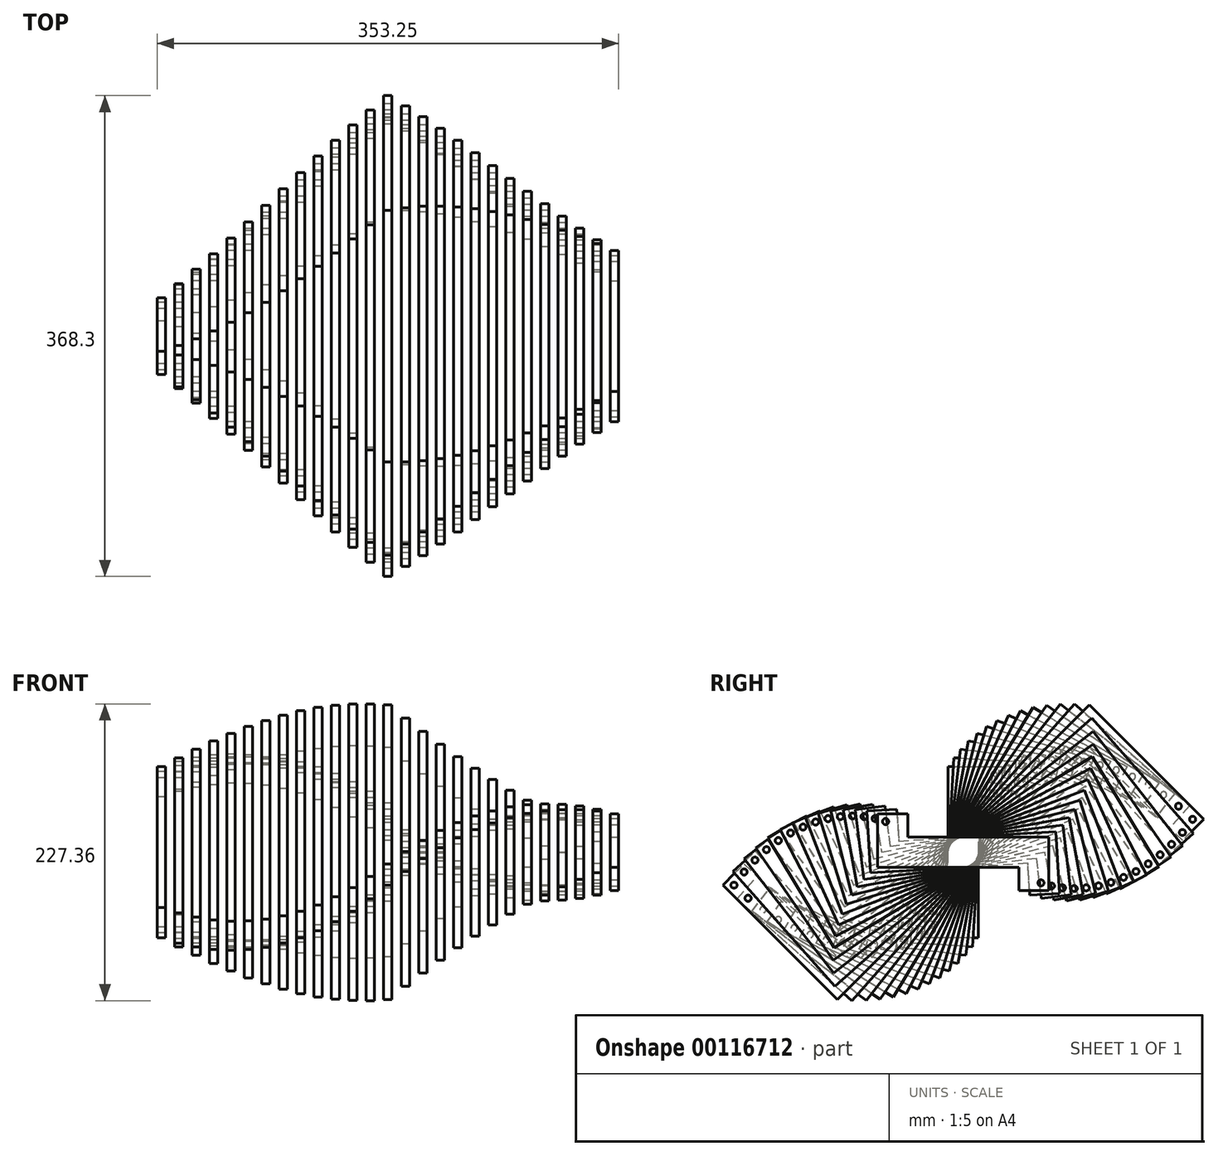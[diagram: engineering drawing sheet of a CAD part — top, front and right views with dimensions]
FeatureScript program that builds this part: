
annotation { "Feature Type Name" : "Feature", "Feature Type Description" : "" }
export const myFeature = defineFeature(function(context is Context, id is Id, definition is map)
    precondition{}
    {
        {
            var Q0;
            Q0=qCreatedBy(makeId("Top.planeOp"),FACE);
            var sketch = newSketch(context, id + "F0", { "sketchPlane" : qUnion([Q0])});
            skLineSegment(sketch, "E0", {"start": v(84.8, 0) * mm, "end": v(-72.92, 0) * mm});
            skSolve(sketch);
        }
        {
            assignVariable(context, id + "F1", {"name" : "Offset", "anyValue" : 13.35});
        }
        {
            assignVariable(context, id + "F2", {"name" : "thick", "anyValue" : 6.35});
        }
        {
            var Q0;
            Q0=qCreatedBy(makeId("Right.planeOp"),FACE);
            var sketch = newSketch(context, id + "F3", { "sketchPlane" : qUnion([Q0])});
            skLineSegment(sketch, "E1", {"start": v(-11.5, 65.5) * mm, "end": v(29.5, 65.5) * mm});
            skLineSegment(sketch, "E2", {"start": v(29.5, 65.5) * mm, "end": v(29.5, 42.5) * mm});
            skLineSegment(sketch, "E3", {"start": v(29.5, 42.5) * mm, "end": v(11.5, 42.5) * mm});
            skLineSegment(sketch, "E4", {"start": v(11.5, 42.5) * mm, "end": v(11.5, -65.5) * mm});
            skLineSegment(sketch, "E5", {"start": v(11.5, -65.5) * mm, "end": v(-29.5, -65.5) * mm});
            skLineSegment(sketch, "E6", {"start": v(-29.5, -65.5) * mm, "end": v(-29.5, -42.5) * mm});
            skLineSegment(sketch, "E7", {"start": v(-29.5, -42.5) * mm, "end": v(-11.5, -42.5) * mm});
            skLineSegment(sketch, "E8", {"start": v(-11.5, -42.5) * mm, "end": v(-11.5, 65.5) * mm});
            skCircle(sketch, "E9", {"center": v(23.5, 59.5) * mm, "radius": 2.35 * mm});
            skLineSegment(sketch, "E10", {"start": v(0, 0) * mm, "end": v(0, 67.87) * mm, "construction": true});
            skCircle(sketch, "E11", {"center": v(-23.5, -59.5) * mm, "radius": 2.35 * mm});
            skSolve(sketch);
        }
        {
            var Q0;
            Q0 = qSketchRegion(id + "F3", true);
            extrude(context, id + "F4", {"entities" : qUnion([Q0]), "depth" : (getVariable(context, 'thick')) * mm});
        }
        {
            var Q0;
            Q0=makeQuery(id+"F4.opExtrude","SWEPT_BODY",BODY,{"disambiguationData":[OSD([sQuery(id+"F3.wireOp",EDGE,"E1"),sQuery(id+"F3.wireOp",EDGE,"E2"),sQuery(id+"F3.wireOp",EDGE,"E3"),sQuery(id+"F3.wireOp",EDGE,"E4"),sQuery(id+"F3.wireOp",EDGE,"E5"),sQuery(id+"F3.wireOp",EDGE,"E6"),sQuery(id+"F3.wireOp",EDGE,"E7"),sQuery(id+"F3.wireOp",EDGE,"E8"),sQuery(id+"F3.wireOp",EDGE,"E9"),sQuery(id+"F3.wireOp",EDGE,"wddxKbAf-IZNn-VG4E-iYQQ-BvLUxmLPDBUU")])]});
            transform(context, id + "F5", {"entities" : qUnion([Q0]), "transformType" : TransformType.TRANSLATION_3D, "dx" : .1 * mm, "dy" : 0 * mm, "dz" : 0 * mm, "makeCopy" : false});
        }
        {
            var Q0;
            Q0=qCreatedBy(makeId("Right.planeOp"),FACE);
            cPlane(context, id + "F6", {"entities" : qUnion([Q0]), "cplaneType" : CPlaneType.OFFSET, "offset" : (getVariable(context, 'Offset')) * mm, "width" : 150 * mm, "height" : 150 * mm});
        }
        {
            var Q0;
            Q0=qCreatedBy(id+"F6.planeOp",FACE);
            var sketch = newSketch(context, id + "F7", { "sketchPlane" : qUnion([Q0])});
            skLineSegment(sketch, "E12", {"start": v(-11.5, 71.85) * mm, "end": v(35.88, 71.85) * mm});
            skLineSegment(sketch, "E13", {"start": v(35.88, 71.85) * mm, "end": v(35.88, 48.85) * mm});
            skLineSegment(sketch, "E14", {"start": v(35.88, 48.85) * mm, "end": v(11.5, 48.85) * mm});
            skLineSegment(sketch, "E15", {"start": v(11.5, 48.85) * mm, "end": v(11.5, -71.85) * mm});
            skLineSegment(sketch, "E16", {"start": v(11.5, -71.85) * mm, "end": v(-35.88, -71.85) * mm});
            skLineSegment(sketch, "E17", {"start": v(-35.88, -71.85) * mm, "end": v(-35.88, -48.84) * mm});
            skLineSegment(sketch, "E18", {"start": v(-35.88, -48.84) * mm, "end": v(-11.5, -48.84) * mm});
            skLineSegment(sketch, "E19", {"start": v(-11.5, -48.84) * mm, "end": v(-11.5, 71.85) * mm});
            skCircle(sketch, "E20", {"center": v(29.88, 65.84) * mm, "radius": 2.35 * mm});
            skCircle(sketch, "E21", {"center": v(-29.88, -65.84) * mm, "radius": 2.35 * mm});
            skSolve(sketch);
        }
        {
            var Q0;
            Q0 = qSketchRegion(id + "F7", true);
            extrude(context, id + "F8", {"entities" : qUnion([Q0]), "depth" : (getVariable(context, 'thick')) * mm});
        }
        {
            var Q0;
            Q0=makeQuery(id+"F8.opExtrude","SWEPT_BODY",BODY,{"disambiguationData":[OSD([sQuery(id+"F7.wireOp",EDGE,"E12"),sQuery(id+"F7.wireOp",EDGE,"E13"),sQuery(id+"F7.wireOp",EDGE,"E14"),sQuery(id+"F7.wireOp",EDGE,"E15"),sQuery(id+"F7.wireOp",EDGE,"E16"),sQuery(id+"F7.wireOp",EDGE,"E17"),sQuery(id+"F7.wireOp",EDGE,"E18"),sQuery(id+"F7.wireOp",EDGE,"E19")])]});
            var Q1;
            Q1=sQuery(id+"F0.wireOp",EDGE,"E0");
            transform(context, id + "F9", {"entities" : qUnion([Q0]), "transformType" : TransformType.ROTATION, "transformAxis" : qUnion([Q1]), "angle" : 3.46 * degree, "makeCopy" : false});
        }
        {
            var Q0;
            Q0=qCreatedBy(id+"F6.planeOp",FACE);
            cPlane(context, id + "F10", {"entities" : qUnion([Q0]), "cplaneType" : CPlaneType.OFFSET, "offset" : (getVariable(context, 'Offset')) * mm, "width" : 150 * mm, "height" : 150 * mm});
        }
        {
            var Q0;
            Q0=qCreatedBy(id+"F10.planeOp",FACE);
            var sketch = newSketch(context, id + "F11", { "sketchPlane" : qUnion([Q0])});
            skLineSegment(sketch, "E22", {"start": v(-11.5, 78.2) * mm, "end": v(42.26, 78.2) * mm});
            skLineSegment(sketch, "E23", {"start": v(42.26, 78.2) * mm, "end": v(42.26, 55.2) * mm});
            skLineSegment(sketch, "E24", {"start": v(42.26, 55.2) * mm, "end": v(11.5, 55.2) * mm});
            skLineSegment(sketch, "E25", {"start": v(11.5, 55.2) * mm, "end": v(11.5, -78.2) * mm});
            skLineSegment(sketch, "E26", {"start": v(11.5, -78.2) * mm, "end": v(-42.26, -78.2) * mm});
            skLineSegment(sketch, "E27", {"start": v(-42.26, -78.2) * mm, "end": v(-42.26, -55.2) * mm});
            skLineSegment(sketch, "E28", {"start": v(-42.26, -55.2) * mm, "end": v(-11.5, -55.2) * mm});
            skLineSegment(sketch, "E29", {"start": v(-11.5, -55.2) * mm, "end": v(-11.5, 78.2) * mm});
            skCircle(sketch, "E30", {"center": v(36.26, 72.2) * mm, "radius": 2.35 * mm});
            skCircle(sketch, "E31", {"center": v(-36.26, -72.2) * mm, "radius": 2.35 * mm});
            skSolve(sketch);
        }
        {
            var Q0;
            Q0 = qSketchRegion(id + "F11", true);
            extrude(context, id + "F12", {"entities" : qUnion([Q0]), "depth" : (getVariable(context, 'thick')) * mm});
        }
        {
            var Q0;
            Q0=makeQuery(id+"F12.opExtrude","SWEPT_BODY",BODY,{"disambiguationData":[OSD([sQuery(id+"F11.wireOp",EDGE,"E22"),sQuery(id+"F11.wireOp",EDGE,"E23"),sQuery(id+"F11.wireOp",EDGE,"E24"),sQuery(id+"F11.wireOp",EDGE,"E25"),sQuery(id+"F11.wireOp",EDGE,"E26"),sQuery(id+"F11.wireOp",EDGE,"E27"),sQuery(id+"F11.wireOp",EDGE,"E28"),sQuery(id+"F11.wireOp",EDGE,"E29")])]});
            var Q1;
            Q1=sQuery(id+"F0.wireOp",EDGE,"E0");
            transform(context, id + "F13", {"entities" : qUnion([Q0]), "transformType" : TransformType.ROTATION, "transformAxis" : qUnion([Q1]), "angle" : 6.92 * degree, "makeCopy" : false});
        }
        {
            var Q0;
            Q0=qCreatedBy(id+"F10.planeOp",FACE);
            cPlane(context, id + "F14", {"entities" : qUnion([Q0]), "cplaneType" : CPlaneType.OFFSET, "offset" : (getVariable(context, 'Offset')) * mm, "width" : 150 * mm, "height" : 150 * mm});
        }
        {
            var Q0;
            Q0=qCreatedBy(id+"F14.planeOp",FACE);
            var sketch = newSketch(context, id + "F15", { "sketchPlane" : qUnion([Q0])});
            skLineSegment(sketch, "E32", {"start": v(-11.5, 84.53) * mm, "end": v(48.64, 84.53) * mm});
            skLineSegment(sketch, "E33", {"start": v(48.64, 84.53) * mm, "end": v(48.64, 61.54) * mm});
            skLineSegment(sketch, "E34", {"start": v(48.64, 61.54) * mm, "end": v(11.5, 61.54) * mm});
            skLineSegment(sketch, "E35", {"start": v(11.5, 61.54) * mm, "end": v(11.5, -84.53) * mm});
            skLineSegment(sketch, "E36", {"start": v(11.5, -84.53) * mm, "end": v(-48.64, -84.53) * mm});
            skLineSegment(sketch, "E37", {"start": v(-48.64, -84.53) * mm, "end": v(-48.64, -61.54) * mm});
            skLineSegment(sketch, "E38", {"start": v(-48.64, -61.54) * mm, "end": v(-11.5, -61.54) * mm});
            skLineSegment(sketch, "E39", {"start": v(-11.5, -61.53) * mm, "end": v(-11.5, 84.53) * mm});
            skCircle(sketch, "E40", {"center": v(42.64, 78.53) * mm, "radius": 2.35 * mm});
            skCircle(sketch, "E41", {"center": v(-42.64, -78.53) * mm, "radius": 2.35 * mm});
            skSolve(sketch);
        }
        {
            var Q0;
            Q0 = qSketchRegion(id + "F15", true);
            extrude(context, id + "F16", {"entities" : qUnion([Q0]), "depth" : (getVariable(context, 'thick')) * mm});
        }
        {
            var Q0;
            Q0=makeQuery(id+"F16.opExtrude","SWEPT_BODY",BODY,{"disambiguationData":[OSD([sQuery(id+"F15.wireOp",EDGE,"E32"),sQuery(id+"F15.wireOp",EDGE,"E33"),sQuery(id+"F15.wireOp",EDGE,"E34"),sQuery(id+"F15.wireOp",EDGE,"E35"),sQuery(id+"F15.wireOp",EDGE,"E36"),sQuery(id+"F15.wireOp",EDGE,"E37"),sQuery(id+"F15.wireOp",EDGE,"E38"),sQuery(id+"F15.wireOp",EDGE,"E39"),sQuery(id+"F15.wireOp",EDGE,"E40")])]});
            var Q1;
            Q1=sQuery(id+"F0.wireOp",EDGE,"E0");
            transform(context, id + "F17", {"entities" : qUnion([Q0]), "transformType" : TransformType.ROTATION, "transformAxis" : qUnion([Q1]), "angle" : 10.38 * degree, "makeCopy" : false});
        }
        {
            var Q0;
            Q0=qCreatedBy(id+"F14.planeOp",FACE);
            cPlane(context, id + "F18", {"entities" : qUnion([Q0]), "cplaneType" : CPlaneType.OFFSET, "offset" : (getVariable(context, 'Offset')) * mm, "width" : 150 * mm, "height" : 150 * mm});
        }
        {
            var Q0;
            Q0=qCreatedBy(id+"F18.planeOp",FACE);
            var sketch = newSketch(context, id + "F19", { "sketchPlane" : qUnion([Q0])});
            skLineSegment(sketch, "E42", {"start": v(-11.5, 90.89) * mm, "end": v(55.02, 90.89) * mm});
            skLineSegment(sketch, "E43", {"start": v(55.02, 90.88) * mm, "end": v(55.02, 67.89) * mm});
            skLineSegment(sketch, "E44", {"start": v(55.02, 67.89) * mm, "end": v(11.5, 67.89) * mm});
            skLineSegment(sketch, "E45", {"start": v(11.5, 67.89) * mm, "end": v(11.5, -90.89) * mm});
            skLineSegment(sketch, "E46", {"start": v(11.5, -90.89) * mm, "end": v(-55.02, -90.89) * mm});
            skLineSegment(sketch, "E47", {"start": v(-55.02, -90.89) * mm, "end": v(-55.02, -67.89) * mm});
            skLineSegment(sketch, "E48", {"start": v(-55.02, -67.89) * mm, "end": v(-11.5, -67.89) * mm});
            skLineSegment(sketch, "E49", {"start": v(-11.5, -67.89) * mm, "end": v(-11.5, 90.89) * mm});
            skCircle(sketch, "E50", {"center": v(49.02, 84.89) * mm, "radius": 2.35 * mm});
            skCircle(sketch, "E51", {"center": v(-49.02, -84.89) * mm, "radius": 2.35 * mm});
            skSolve(sketch);
        }
        {
            var Q0;
            Q0 = qSketchRegion(id + "F19", true);
            extrude(context, id + "F20", {"entities" : qUnion([Q0]), "depth" : (getVariable(context, 'thick')) * mm});
        }
        {
            var Q0;
            Q0=makeQuery(id+"F20.opExtrude","SWEPT_BODY",BODY,{"disambiguationData":[OSD([sQuery(id+"F19.wireOp",EDGE,"E42"),sQuery(id+"F19.wireOp",EDGE,"E43"),sQuery(id+"F19.wireOp",EDGE,"E44"),sQuery(id+"F19.wireOp",EDGE,"E45"),sQuery(id+"F19.wireOp",EDGE,"E46"),sQuery(id+"F19.wireOp",EDGE,"E47"),sQuery(id+"F19.wireOp",EDGE,"E48"),sQuery(id+"F19.wireOp",EDGE,"E49"),sQuery(id+"F19.wireOp",EDGE,"E50")])]});
            var Q1;
            Q1=sQuery(id+"F0.wireOp",EDGE,"E0");
            transform(context, id + "F21", {"entities" : qUnion([Q0]), "transformType" : TransformType.ROTATION, "transformAxis" : qUnion([Q1]), "angle" : 13.84 * degree, "makeCopy" : false});
        }
        {
            var Q0;
            Q0=qCreatedBy(id+"F18.planeOp",FACE);
            cPlane(context, id + "F22", {"entities" : qUnion([Q0]), "cplaneType" : CPlaneType.OFFSET, "offset" : (getVariable(context, 'Offset')) * mm, "width" : 150 * mm, "height" : 150 * mm});
        }
        {
            var Q0;
            Q0=qCreatedBy(id+"F22.planeOp",FACE);
            var sketch = newSketch(context, id + "F23", { "sketchPlane" : qUnion([Q0])});
            skLineSegment(sketch, "E52", {"start": v(-11.5, 97.23) * mm, "end": v(61.4, 97.23) * mm});
            skLineSegment(sketch, "E53", {"start": v(61.4, 97.23) * mm, "end": v(61.4, 74.23) * mm});
            skLineSegment(sketch, "E54", {"start": v(61.4, 74.23) * mm, "end": v(11.5, 74.23) * mm});
            skLineSegment(sketch, "E55", {"start": v(11.5, 74.23) * mm, "end": v(11.5, -97.23) * mm});
            skLineSegment(sketch, "E56", {"start": v(11.5, -97.23) * mm, "end": v(-61.4, -97.23) * mm});
            skLineSegment(sketch, "E57", {"start": v(-61.4, -97.23) * mm, "end": v(-61.4, -74.23) * mm});
            skLineSegment(sketch, "E58", {"start": v(-61.4, -74.23) * mm, "end": v(-11.5, -74.23) * mm});
            skLineSegment(sketch, "E59", {"start": v(-11.5, -74.23) * mm, "end": v(-11.5, 97.23) * mm});
            skCircle(sketch, "E60", {"center": v(55.4, 91.23) * mm, "radius": 2.35 * mm});
            skCircle(sketch, "E61", {"center": v(-55.4, -91.23) * mm, "radius": 2.35 * mm});
            skSolve(sketch);
        }
        {
            var Q0;
            Q0 = qSketchRegion(id + "F23", true);
            extrude(context, id + "F24", {"entities" : qUnion([Q0]), "depth" : (getVariable(context, 'thick')) * mm});
        }
        {
            var Q0;
            Q0=makeQuery(id+"F24.opExtrude","SWEPT_BODY",BODY,{"disambiguationData":[OSD([sQuery(id+"F23.wireOp",EDGE,"E52"),sQuery(id+"F23.wireOp",EDGE,"E53"),sQuery(id+"F23.wireOp",EDGE,"E54"),sQuery(id+"F23.wireOp",EDGE,"E55"),sQuery(id+"F23.wireOp",EDGE,"E56"),sQuery(id+"F23.wireOp",EDGE,"E57"),sQuery(id+"F23.wireOp",EDGE,"E58"),sQuery(id+"F23.wireOp",EDGE,"E59"),sQuery(id+"F23.wireOp",EDGE,"E60")])]});
            var Q1;
            Q1=sQuery(id+"F0.wireOp",EDGE,"E0");
            transform(context, id + "F25", {"entities" : qUnion([Q0]), "transformType" : TransformType.ROTATION, "transformAxis" : qUnion([Q1]), "angle" : 17.3 * degree, "makeCopy" : false});
        }
        {
            var Q0;
            Q0=qCreatedBy(id+"F22.planeOp",FACE);
            cPlane(context, id + "F26", {"entities" : qUnion([Q0]), "cplaneType" : CPlaneType.OFFSET, "offset" : (getVariable(context, 'Offset')) * mm, "width" : 150 * mm, "height" : 150 * mm});
        }
        {
            var Q0;
            Q0=qCreatedBy(id+"F26.planeOp",FACE);
            var sketch = newSketch(context, id + "F27", { "sketchPlane" : qUnion([Q0])});
            skLineSegment(sketch, "E62", {"start": v(-11.5, 103.58) * mm, "end": v(67.78, 103.58) * mm});
            skLineSegment(sketch, "E63", {"start": v(67.78, 103.58) * mm, "end": v(67.78, 80.57) * mm});
            skLineSegment(sketch, "E64", {"start": v(67.78, 80.57) * mm, "end": v(11.5, 80.57) * mm});
            skLineSegment(sketch, "E65", {"start": v(11.5, 80.57) * mm, "end": v(11.5, -103.58) * mm});
            skLineSegment(sketch, "E66", {"start": v(11.5, -103.58) * mm, "end": v(-67.78, -103.58) * mm});
            skLineSegment(sketch, "E67", {"start": v(-67.78, -103.58) * mm, "end": v(-67.78, -80.57) * mm});
            skLineSegment(sketch, "E68", {"start": v(-67.78, -80.57) * mm, "end": v(-11.5, -80.57) * mm});
            skLineSegment(sketch, "E69", {"start": v(-11.5, -80.57) * mm, "end": v(-11.5, 103.58) * mm});
            skCircle(sketch, "E70", {"center": v(61.78, 97.58) * mm, "radius": 2.35 * mm});
            skCircle(sketch, "E71", {"center": v(-61.78, -97.58) * mm, "radius": 2.35 * mm});
            skSolve(sketch);
        }
        {
            var Q0;
            Q0 = qSketchRegion(id + "F27", true);
            extrude(context, id + "F28", {"entities" : qUnion([Q0]), "depth" : (getVariable(context, 'thick')) * mm});
        }
        {
            var Q0;
            Q0=makeQuery(id+"F28.opExtrude","SWEPT_BODY",BODY,{"disambiguationData":[OSD([sQuery(id+"F27.wireOp",EDGE,"E62"),sQuery(id+"F27.wireOp",EDGE,"E63"),sQuery(id+"F27.wireOp",EDGE,"E64"),sQuery(id+"F27.wireOp",EDGE,"E65"),sQuery(id+"F27.wireOp",EDGE,"E66"),sQuery(id+"F27.wireOp",EDGE,"E67"),sQuery(id+"F27.wireOp",EDGE,"E68"),sQuery(id+"F27.wireOp",EDGE,"E69"),sQuery(id+"F27.wireOp",EDGE,"E70")])]});
            var Q1;
            Q1=sQuery(id+"F0.wireOp",EDGE,"E0");
            transform(context, id + "F29", {"entities" : qUnion([Q0]), "transformType" : TransformType.ROTATION, "transformAxis" : qUnion([Q1]), "angle" : 20.76 * degree, "makeCopy" : false});
        }
        {
            var Q0;
            Q0=qCreatedBy(id+"F26.planeOp",FACE);
            cPlane(context, id + "F30", {"entities" : qUnion([Q0]), "cplaneType" : CPlaneType.OFFSET, "offset" : (getVariable(context, 'Offset')) * mm, "width" : 150 * mm, "height" : 150 * mm});
        }
        {
            var Q0;
            Q0=qCreatedBy(id+"F30.planeOp",FACE);
            var sketch = newSketch(context, id + "F31", { "sketchPlane" : qUnion([Q0])});
            skLineSegment(sketch, "E72", {"start": v(-11.5, 109.92) * mm, "end": v(74.16, 109.92) * mm});
            skLineSegment(sketch, "E73", {"start": v(74.16, 109.92) * mm, "end": v(74.16, 86.92) * mm});
            skLineSegment(sketch, "E74", {"start": v(74.16, 86.92) * mm, "end": v(11.5, 86.92) * mm});
            skLineSegment(sketch, "E75", {"start": v(11.5, 86.92) * mm, "end": v(11.5, -109.92) * mm});
            skLineSegment(sketch, "E76", {"start": v(11.5, -109.92) * mm, "end": v(-74.16, -109.92) * mm});
            skLineSegment(sketch, "E77", {"start": v(-74.16, -109.92) * mm, "end": v(-74.16, -86.92) * mm});
            skLineSegment(sketch, "E78", {"start": v(-74.16, -86.92) * mm, "end": v(-11.5, -86.92) * mm});
            skLineSegment(sketch, "E79", {"start": v(-11.5, -86.92) * mm, "end": v(-11.5, 109.92) * mm});
            skCircle(sketch, "E80", {"center": v(68.16, 103.92) * mm, "radius": 2.35 * mm});
            skCircle(sketch, "E81", {"center": v(-68.16, -103.92) * mm, "radius": 2.35 * mm});
            skSolve(sketch);
        }
        {
            var Q0;
            Q0 = qSketchRegion(id + "F31", true);
            extrude(context, id + "F32", {"entities" : qUnion([Q0]), "depth" : (getVariable(context, 'thick')) * mm});
        }
        {
            var Q0;
            Q0=makeQuery(id+"F32.opExtrude","SWEPT_BODY",BODY,{"disambiguationData":[OSD([sQuery(id+"F31.wireOp",EDGE,"E72"),sQuery(id+"F31.wireOp",EDGE,"E73"),sQuery(id+"F31.wireOp",EDGE,"E74"),sQuery(id+"F31.wireOp",EDGE,"E75"),sQuery(id+"F31.wireOp",EDGE,"E76"),sQuery(id+"F31.wireOp",EDGE,"E77"),sQuery(id+"F31.wireOp",EDGE,"E78"),sQuery(id+"F31.wireOp",EDGE,"E79"),sQuery(id+"F31.wireOp",EDGE,"E80")])]});
            var Q1;
            Q1=sQuery(id+"F0.wireOp",EDGE,"E0");
            transform(context, id + "F33", {"entities" : qUnion([Q0]), "transformType" : TransformType.ROTATION, "transformAxis" : qUnion([Q1]), "angle" : 24.22 * degree, "makeCopy" : false});
        }
        {
            var Q0;
            Q0=qCreatedBy(id+"F30.planeOp",FACE);
            cPlane(context, id + "F34", {"entities" : qUnion([Q0]), "cplaneType" : CPlaneType.OFFSET, "offset" : (getVariable(context, 'Offset')) * mm, "width" : 150 * mm, "height" : 150 * mm});
        }
        {
            var Q0;
            Q0=qCreatedBy(id+"F34.planeOp",FACE);
            var sketch = newSketch(context, id + "F35", { "sketchPlane" : qUnion([Q0])});
            skLineSegment(sketch, "E82", {"start": v(-11.5, 116.27) * mm, "end": v(80.54, 116.27) * mm});
            skLineSegment(sketch, "E83", {"start": v(80.54, 116.27) * mm, "end": v(80.54, 93.27) * mm});
            skLineSegment(sketch, "E84", {"start": v(80.54, 93.27) * mm, "end": v(11.5, 93.27) * mm});
            skLineSegment(sketch, "E85", {"start": v(11.5, 93.27) * mm, "end": v(11.5, -116.27) * mm});
            skLineSegment(sketch, "E86", {"start": v(11.5, -116.27) * mm, "end": v(-80.54, -116.27) * mm});
            skLineSegment(sketch, "E87", {"start": v(-80.54, -116.27) * mm, "end": v(-80.54, -93.27) * mm});
            skLineSegment(sketch, "E88", {"start": v(-80.54, -93.27) * mm, "end": v(-11.5, -93.27) * mm});
            skLineSegment(sketch, "E89", {"start": v(-11.5, -93.27) * mm, "end": v(-11.5, 116.27) * mm});
            skCircle(sketch, "E90", {"center": v(74.54, 110.27) * mm, "radius": 2.35 * mm});
            skCircle(sketch, "E91", {"center": v(-74.54, -110.27) * mm, "radius": 2.35 * mm});
            skSolve(sketch);
        }
        {
            var Q0;
            Q0 = qSketchRegion(id + "F35", true);
            extrude(context, id + "F36", {"entities" : qUnion([Q0]), "depth" : (getVariable(context, 'thick')) * mm});
        }
        {
            var Q0;
            Q0=makeQuery(id+"F36.opExtrude","SWEPT_BODY",BODY,{"disambiguationData":[OSD([sQuery(id+"F35.wireOp",EDGE,"E82"),sQuery(id+"F35.wireOp",EDGE,"E83"),sQuery(id+"F35.wireOp",EDGE,"E84"),sQuery(id+"F35.wireOp",EDGE,"E85"),sQuery(id+"F35.wireOp",EDGE,"E86"),sQuery(id+"F35.wireOp",EDGE,"E87"),sQuery(id+"F35.wireOp",EDGE,"E88"),sQuery(id+"F35.wireOp",EDGE,"E89"),sQuery(id+"F35.wireOp",EDGE,"E90")])]});
            var Q1;
            Q1=sQuery(id+"F0.wireOp",EDGE,"E0");
            transform(context, id + "F37", {"entities" : qUnion([Q0]), "transformType" : TransformType.ROTATION, "transformAxis" : qUnion([Q1]), "angle" : 27.68 * degree, "makeCopy" : false});
        }
        {
            var Q0;
            Q0=qCreatedBy(id+"F34.planeOp",FACE);
            cPlane(context, id + "F38", {"entities" : qUnion([Q0]), "cplaneType" : CPlaneType.OFFSET, "offset" : (getVariable(context, 'Offset')) * mm, "width" : 150 * mm, "height" : 150 * mm});
        }
        {
            var Q0;
            Q0=qCreatedBy(id+"F38.planeOp",FACE);
            var sketch = newSketch(context, id + "F39", { "sketchPlane" : qUnion([Q0])});
            skLineSegment(sketch, "E92", {"start": v(-11.5, 122.61) * mm, "end": v(86.92, 122.61) * mm});
            skLineSegment(sketch, "E93", {"start": v(86.92, 122.61) * mm, "end": v(86.92, 99.62) * mm});
            skLineSegment(sketch, "E94", {"start": v(86.92, 99.62) * mm, "end": v(11.5, 99.61) * mm});
            skLineSegment(sketch, "E95", {"start": v(11.5, 99.61) * mm, "end": v(11.5, -122.61) * mm});
            skLineSegment(sketch, "E96", {"start": v(11.5, -122.61) * mm, "end": v(-86.92, -122.62) * mm});
            skLineSegment(sketch, "E97", {"start": v(-86.92, -122.62) * mm, "end": v(-86.92, -99.61) * mm});
            skLineSegment(sketch, "E98", {"start": v(-86.92, -99.61) * mm, "end": v(-11.5, -99.61) * mm});
            skLineSegment(sketch, "E99", {"start": v(-11.5, -99.61) * mm, "end": v(-11.5, 122.62) * mm});
            skCircle(sketch, "E100", {"center": v(80.92, 116.61) * mm, "radius": 2.35 * mm});
            skCircle(sketch, "E101", {"center": v(-80.92, -116.62) * mm, "radius": 2.35 * mm});
            skSolve(sketch);
        }
        {
            var Q0;
            Q0 = qSketchRegion(id + "F39", true);
            extrude(context, id + "F40", {"entities" : qUnion([Q0]), "depth" : (getVariable(context, 'thick')) * mm});
        }
        {
            var Q0;
            Q0=makeQuery(id+"F40.opExtrude","SWEPT_BODY",BODY,{"disambiguationData":[OSD([sQuery(id+"F39.wireOp",EDGE,"E92"),sQuery(id+"F39.wireOp",EDGE,"E93"),sQuery(id+"F39.wireOp",EDGE,"E94"),sQuery(id+"F39.wireOp",EDGE,"E95"),sQuery(id+"F39.wireOp",EDGE,"E96"),sQuery(id+"F39.wireOp",EDGE,"E97"),sQuery(id+"F39.wireOp",EDGE,"E98"),sQuery(id+"F39.wireOp",EDGE,"E99"),sQuery(id+"F39.wireOp",EDGE,"E100")])]});
            var Q1;
            Q1=sQuery(id+"F0.wireOp",EDGE,"E0");
            transform(context, id + "F41", {"entities" : qUnion([Q0]), "transformType" : TransformType.ROTATION, "transformAxis" : qUnion([Q1]), "angle" : 31.14 * degree, "makeCopy" : false});
        }
        {
            var Q0;
            Q0=qCreatedBy(id+"F38.planeOp",FACE);
            cPlane(context, id + "F42", {"entities" : qUnion([Q0]), "cplaneType" : CPlaneType.OFFSET, "offset" : (getVariable(context, 'Offset')) * mm, "width" : 150 * mm, "height" : 150 * mm});
        }
        {
            var Q0;
            Q0=qCreatedBy(id+"F42.planeOp",FACE);
            var sketch = newSketch(context, id + "F43", { "sketchPlane" : qUnion([Q0])});
            skLineSegment(sketch, "E102", {"start": v(-11.5, 128.96) * mm, "end": v(93.3, 128.96) * mm});
            skLineSegment(sketch, "E103", {"start": v(93.3, 128.96) * mm, "end": v(93.3, 105.96) * mm});
            skLineSegment(sketch, "E104", {"start": v(93.3, 105.96) * mm, "end": v(11.5, 105.96) * mm});
            skLineSegment(sketch, "E105", {"start": v(11.5, 105.96) * mm, "end": v(11.5, -128.96) * mm});
            skLineSegment(sketch, "E106", {"start": v(11.5, -128.96) * mm, "end": v(-93.3, -128.96) * mm});
            skLineSegment(sketch, "E107", {"start": v(-93.3, -128.96) * mm, "end": v(-93.3, -105.96) * mm});
            skLineSegment(sketch, "E108", {"start": v(-93.3, -105.96) * mm, "end": v(-11.5, -105.96) * mm});
            skLineSegment(sketch, "E109", {"start": v(-11.5, -105.96) * mm, "end": v(-11.5, 128.96) * mm});
            skCircle(sketch, "E110", {"center": v(87.3, 122.96) * mm, "radius": 2.35 * mm});
            skCircle(sketch, "E111", {"center": v(-87.3, -122.96) * mm, "radius": 2.35 * mm});
            skSolve(sketch);
        }
        {
            var Q0;
            Q0 = qSketchRegion(id + "F43", true);
            extrude(context, id + "F44", {"entities" : qUnion([Q0]), "depth" : (getVariable(context, 'thick')) * mm});
        }
        {
            var Q0;
            Q0=makeQuery(id+"F44.opExtrude","SWEPT_BODY",BODY,{"disambiguationData":[OSD([sQuery(id+"F43.wireOp",EDGE,"E102"),sQuery(id+"F43.wireOp",EDGE,"E103"),sQuery(id+"F43.wireOp",EDGE,"E104"),sQuery(id+"F43.wireOp",EDGE,"E105"),sQuery(id+"F43.wireOp",EDGE,"E106"),sQuery(id+"F43.wireOp",EDGE,"E107"),sQuery(id+"F43.wireOp",EDGE,"E108"),sQuery(id+"F43.wireOp",EDGE,"E109"),sQuery(id+"F43.wireOp",EDGE,"E110")])]});
            var Q1;
            Q1=sQuery(id+"F0.wireOp",EDGE,"E0");
            transform(context, id + "F45", {"entities" : qUnion([Q0]), "transformType" : TransformType.ROTATION, "transformAxis" : qUnion([Q1]), "angle" : 34.6 * degree, "makeCopy" : false});
        }
        {
            var Q0;
            Q0=qCreatedBy(id+"F42.planeOp",FACE);
            cPlane(context, id + "F46", {"entities" : qUnion([Q0]), "cplaneType" : CPlaneType.OFFSET, "offset" : (getVariable(context, 'Offset')) * mm, "width" : 150 * mm, "height" : 150 * mm});
        }
        {
            var Q0;
            Q0=qCreatedBy(id+"F46.planeOp",FACE);
            var sketch = newSketch(context, id + "F47", { "sketchPlane" : qUnion([Q0])});
            skLineSegment(sketch, "E112", {"start": v(-11.5, 135.3) * mm, "end": v(99.68, 135.3) * mm});
            skLineSegment(sketch, "E113", {"start": v(99.68, 135.3) * mm, "end": v(99.68, 112.3) * mm});
            skLineSegment(sketch, "E114", {"start": v(99.68, 112.3) * mm, "end": v(11.5, 112.3) * mm});
            skLineSegment(sketch, "E115", {"start": v(11.5, 112.3) * mm, "end": v(11.5, -135.3) * mm});
            skLineSegment(sketch, "E116", {"start": v(11.5, -135.3) * mm, "end": v(-99.68, -135.3) * mm});
            skLineSegment(sketch, "E117", {"start": v(-99.68, -135.3) * mm, "end": v(-99.68, -112.3) * mm});
            skLineSegment(sketch, "E118", {"start": v(-99.68, -112.3) * mm, "end": v(-11.5, -112.3) * mm});
            skLineSegment(sketch, "E119", {"start": v(-11.5, -112.3) * mm, "end": v(-11.5, 135.3) * mm});
            skCircle(sketch, "E120", {"center": v(93.68, 129.3) * mm, "radius": 2.35 * mm});
            skCircle(sketch, "E121", {"center": v(-93.68, -129.3) * mm, "radius": 2.35 * mm});
            skSolve(sketch);
        }
        {
            var Q0;
            Q0 = qSketchRegion(id + "F47", true);
            extrude(context, id + "F48", {"entities" : qUnion([Q0]), "depth" : (getVariable(context, 'thick')) * mm});
        }
        {
            var Q0;
            Q0=makeQuery(id+"F48.opExtrude","SWEPT_BODY",BODY,{"disambiguationData":[OSD([sQuery(id+"F47.wireOp",EDGE,"E112"),sQuery(id+"F47.wireOp",EDGE,"E113"),sQuery(id+"F47.wireOp",EDGE,"E114"),sQuery(id+"F47.wireOp",EDGE,"E115"),sQuery(id+"F47.wireOp",EDGE,"E116"),sQuery(id+"F47.wireOp",EDGE,"E117"),sQuery(id+"F47.wireOp",EDGE,"E118"),sQuery(id+"F47.wireOp",EDGE,"E119"),sQuery(id+"F47.wireOp",EDGE,"E120"),sQuery(id+"F47.wireOp",EDGE,"E121")])]});
            var Q1;
            Q1=sQuery(id+"F0.wireOp",EDGE,"E0");
            transform(context, id + "F49", {"entities" : qUnion([Q0]), "transformType" : TransformType.ROTATION, "transformAxis" : qUnion([Q1]), "angle" : 38.06 * degree, "makeCopy" : false});
        }
        {
            var Q0;
            Q0=qCreatedBy(id+"F46.planeOp",FACE);
            cPlane(context, id + "F50", {"entities" : qUnion([Q0]), "cplaneType" : CPlaneType.OFFSET, "offset" : (getVariable(context, 'Offset')) * mm, "width" : 150 * mm, "height" : 150 * mm});
        }
        {
            var Q0;
            Q0=qCreatedBy(id+"F50.planeOp",FACE);
            var sketch = newSketch(context, id + "F51", { "sketchPlane" : qUnion([Q0])});
            skLineSegment(sketch, "E122", {"start": v(-11.5, 141.65) * mm, "end": v(106.06, 141.65) * mm});
            skLineSegment(sketch, "E123", {"start": v(106.06, 141.65) * mm, "end": v(106.06, 118.65) * mm});
            skLineSegment(sketch, "E124", {"start": v(106.06, 118.65) * mm, "end": v(11.5, 118.65) * mm});
            skLineSegment(sketch, "E125", {"start": v(11.5, 118.65) * mm, "end": v(11.5, -141.65) * mm});
            skLineSegment(sketch, "E126", {"start": v(11.5, -141.65) * mm, "end": v(-106.06, -141.65) * mm});
            skLineSegment(sketch, "E127", {"start": v(-106.06, -141.65) * mm, "end": v(-106.06, -118.65) * mm});
            skLineSegment(sketch, "E128", {"start": v(-106.06, -118.65) * mm, "end": v(-11.5, -118.65) * mm});
            skLineSegment(sketch, "E129", {"start": v(-11.5, -118.65) * mm, "end": v(-11.5, 141.65) * mm});
            skCircle(sketch, "E130", {"center": v(100.06, 135.65) * mm, "radius": 2.35 * mm});
            skCircle(sketch, "E131", {"center": v(-100.06, -135.65) * mm, "radius": 2.35 * mm});
            skSolve(sketch);
        }
        {
            var Q0;
            Q0 = qSketchRegion(id + "F51", true);
            extrude(context, id + "F52", {"entities" : qUnion([Q0]), "depth" : (getVariable(context, 'thick')) * mm});
        }
        {
            var Q0;
            Q0=makeQuery(id+"F52.opExtrude","SWEPT_BODY",BODY,{"disambiguationData":[OSD([sQuery(id+"F51.wireOp",EDGE,"E122"),sQuery(id+"F51.wireOp",EDGE,"E123"),sQuery(id+"F51.wireOp",EDGE,"E124"),sQuery(id+"F51.wireOp",EDGE,"E125"),sQuery(id+"F51.wireOp",EDGE,"E126"),sQuery(id+"F51.wireOp",EDGE,"E127"),sQuery(id+"F51.wireOp",EDGE,"E128"),sQuery(id+"F51.wireOp",EDGE,"E129"),sQuery(id+"F51.wireOp",EDGE,"E130"),sQuery(id+"F51.wireOp",EDGE,"E131")])]});
            var Q1;
            Q1=sQuery(id+"F0.wireOp",EDGE,"E0");
            transform(context, id + "F53", {"entities" : qUnion([Q0]), "transformType" : TransformType.ROTATION, "transformAxis" : qUnion([Q1]), "angle" : 41.52 * degree, "makeCopy" : false});
        }
        {
            var Q0;
            Q0=qCreatedBy(id+"F50.planeOp",FACE);
            cPlane(context, id + "F54", {"entities" : qUnion([Q0]), "cplaneType" : CPlaneType.OFFSET, "offset" : (getVariable(context, 'Offset')) * mm, "width" : 150 * mm, "height" : 150 * mm});
        }
        {
            var Q0;
            Q0=qCreatedBy(id+"F54.planeOp",FACE);
            var sketch = newSketch(context, id + "F55", { "sketchPlane" : qUnion([Q0])});
            skLineSegment(sketch, "E132", {"start": v(-11.5, 148) * mm, "end": v(112.44, 148) * mm});
            skLineSegment(sketch, "E133", {"start": v(112.44, 148) * mm, "end": v(112.44, 125) * mm});
            skLineSegment(sketch, "E134", {"start": v(112.44, 125) * mm, "end": v(11.5, 125) * mm});
            skLineSegment(sketch, "E135", {"start": v(11.5, 125) * mm, "end": v(11.5, -148) * mm});
            skLineSegment(sketch, "E136", {"start": v(11.5, -148) * mm, "end": v(-112.44, -148) * mm});
            skLineSegment(sketch, "E137", {"start": v(-112.44, -148) * mm, "end": v(-112.44, -125) * mm});
            skLineSegment(sketch, "E138", {"start": v(-112.44, -125) * mm, "end": v(-11.5, -125) * mm});
            skLineSegment(sketch, "E139", {"start": v(-11.5, -125) * mm, "end": v(-11.5, 148) * mm});
            skCircle(sketch, "E140", {"center": v(106.44, 142) * mm, "radius": 2.35 * mm});
            skCircle(sketch, "E141", {"center": v(-106.44, -142) * mm, "radius": 2.35 * mm});
            skSolve(sketch);
        }
        {
            var Q0;
            Q0 = qSketchRegion(id + "F55", true);
            extrude(context, id + "F56", {"entities" : qUnion([Q0]), "depth" : (getVariable(context, 'thick')) * mm});
        }
        {
            var Q0;
            Q0=makeQuery(id+"F56.opExtrude","SWEPT_BODY",BODY,{"disambiguationData":[OSD([sQuery(id+"F55.wireOp",EDGE,"E132"),sQuery(id+"F55.wireOp",EDGE,"E133"),sQuery(id+"F55.wireOp",EDGE,"E134"),sQuery(id+"F55.wireOp",EDGE,"E135"),sQuery(id+"F55.wireOp",EDGE,"E136"),sQuery(id+"F55.wireOp",EDGE,"E137"),sQuery(id+"F55.wireOp",EDGE,"E138"),sQuery(id+"F55.wireOp",EDGE,"E139"),sQuery(id+"F55.wireOp",EDGE,"E140"),sQuery(id+"F55.wireOp",EDGE,"E141")])]});
            var Q1;
            Q1=sQuery(id+"F0.wireOp",EDGE,"E0");
            transform(context, id + "F57", {"entities" : qUnion([Q0]), "transformType" : TransformType.ROTATION, "transformAxis" : qUnion([Q1]), "angle" : 44.98 * degree, "makeCopy" : false});
        }
        {
            var Q0;
            Q0=makeQuery(id+"F56.opExtrude","CAP_FACE",FACE,{"disambiguationData":[OSD([sQuery(id+"F55.wireOp",EDGE,"E132"),sQuery(id+"F55.wireOp",EDGE,"E133"),sQuery(id+"F55.wireOp",EDGE,"E134"),sQuery(id+"F55.wireOp",EDGE,"E135"),sQuery(id+"F55.wireOp",EDGE,"E136"),sQuery(id+"F55.wireOp",EDGE,"E137"),sQuery(id+"F55.wireOp",EDGE,"E138"),sQuery(id+"F55.wireOp",EDGE,"E139"),sQuery(id+"F55.wireOp",EDGE,"E140"),sQuery(id+"F55.wireOp",EDGE,"E141")])],"isStart":false});
            cPlane(context, id + "F58", {"entities" : qUnion([Q0]), "cplaneType" : CPlaneType.OFFSET, "offset" : (getVariable(context, 'thick') / 2) * mm, "oppositeDirection" : true, "width" : 150 * mm, "height" : 150 * mm});
        }
        {
            var Q0;
            Q0=makeQuery(id+"F52.opExtrude","SWEPT_BODY",BODY,{"disambiguationData":[OSD([sQuery(id+"F51.wireOp",EDGE,"E122"),sQuery(id+"F51.wireOp",EDGE,"E123"),sQuery(id+"F51.wireOp",EDGE,"E124"),sQuery(id+"F51.wireOp",EDGE,"E125"),sQuery(id+"F51.wireOp",EDGE,"E126"),sQuery(id+"F51.wireOp",EDGE,"E127"),sQuery(id+"F51.wireOp",EDGE,"E128"),sQuery(id+"F51.wireOp",EDGE,"E129"),sQuery(id+"F51.wireOp",EDGE,"E130"),sQuery(id+"F51.wireOp",EDGE,"E131")])]});
            var Q1;
            Q1=qCreatedBy(id+"F58.planeOp",FACE);
            mirror(context, id + "F59", {"entities" : qUnion([Q0]), "mirrorPlane" : qUnion([Q1])});
        }
        {
            var Q0;
            Q0=makeQuery(id+"F59.opPattern","COPY",BODY,{"derivedFrom":makeQuery(id+"F52.opExtrude","SWEPT_BODY",BODY,{"disambiguationData":[OSD([sQuery(id+"F51.wireOp",EDGE,"E122"),sQuery(id+"F51.wireOp",EDGE,"E123"),sQuery(id+"F51.wireOp",EDGE,"E124"),sQuery(id+"F51.wireOp",EDGE,"E125"),sQuery(id+"F51.wireOp",EDGE,"E126"),sQuery(id+"F51.wireOp",EDGE,"E127"),sQuery(id+"F51.wireOp",EDGE,"E128"),sQuery(id+"F51.wireOp",EDGE,"E129"),sQuery(id+"F51.wireOp",EDGE,"E130"),sQuery(id+"F51.wireOp",EDGE,"E131")])]}),"instanceName":"1"});
            var Q1;
            Q1=sQuery(id+"F0.wireOp",EDGE,"E0");
            transform(context, id + "F60", {"entities" : qUnion([Q0]), "transformType" : TransformType.ROTATION, "transformAxis" : qUnion([Q1]), "angle" : 6.92 * degree, "makeCopy" : false});
        }
        {
            var Q0;
            Q0=makeQuery(id+"F48.opExtrude","SWEPT_BODY",BODY,{"disambiguationData":[OSD([sQuery(id+"F47.wireOp",EDGE,"E112"),sQuery(id+"F47.wireOp",EDGE,"E113"),sQuery(id+"F47.wireOp",EDGE,"E114"),sQuery(id+"F47.wireOp",EDGE,"E115"),sQuery(id+"F47.wireOp",EDGE,"E116"),sQuery(id+"F47.wireOp",EDGE,"E117"),sQuery(id+"F47.wireOp",EDGE,"E118"),sQuery(id+"F47.wireOp",EDGE,"E119"),sQuery(id+"F47.wireOp",EDGE,"E120"),sQuery(id+"F47.wireOp",EDGE,"E121")])]});
            var Q1;
            Q1=qCreatedBy(id+"F58.planeOp",FACE);
            mirror(context, id + "F61", {"entities" : qUnion([Q0]), "mirrorPlane" : qUnion([Q1])});
        }
        {
            var Q0;
            Q0=makeQuery(id+"F61.opPattern","COPY",BODY,{"derivedFrom":makeQuery(id+"F48.opExtrude","SWEPT_BODY",BODY,{"disambiguationData":[OSD([sQuery(id+"F47.wireOp",EDGE,"E112"),sQuery(id+"F47.wireOp",EDGE,"E113"),sQuery(id+"F47.wireOp",EDGE,"E114"),sQuery(id+"F47.wireOp",EDGE,"E115"),sQuery(id+"F47.wireOp",EDGE,"E116"),sQuery(id+"F47.wireOp",EDGE,"E117"),sQuery(id+"F47.wireOp",EDGE,"E118"),sQuery(id+"F47.wireOp",EDGE,"E119"),sQuery(id+"F47.wireOp",EDGE,"E120"),sQuery(id+"F47.wireOp",EDGE,"E121")])]}),"instanceName":"1"});
            var Q1;
            Q1=sQuery(id+"F0.wireOp",EDGE,"E0");
            transform(context, id + "F62", {"entities" : qUnion([Q0]), "transformType" : TransformType.ROTATION, "transformAxis" : qUnion([Q1]), "angle" : 13.85 * degree, "makeCopy" : false});
        }
        {
            var Q0;
            Q0=makeQuery(id+"F44.opExtrude","SWEPT_BODY",BODY,{"disambiguationData":[OSD([sQuery(id+"F43.wireOp",EDGE,"E102"),sQuery(id+"F43.wireOp",EDGE,"E103"),sQuery(id+"F43.wireOp",EDGE,"E104"),sQuery(id+"F43.wireOp",EDGE,"E105"),sQuery(id+"F43.wireOp",EDGE,"E106"),sQuery(id+"F43.wireOp",EDGE,"E107"),sQuery(id+"F43.wireOp",EDGE,"E108"),sQuery(id+"F43.wireOp",EDGE,"E109"),sQuery(id+"F43.wireOp",EDGE,"E110"),sQuery(id+"F43.wireOp",EDGE,"E111")])]});
            var Q1;
            Q1=qCreatedBy(id+"F58.planeOp",FACE);
            mirror(context, id + "F63", {"entities" : qUnion([Q0]), "mirrorPlane" : qUnion([Q1])});
        }
        {
            var Q0;
            Q0=makeQuery(id+"F63.opPattern","COPY",BODY,{"derivedFrom":makeQuery(id+"F44.opExtrude","SWEPT_BODY",BODY,{"disambiguationData":[OSD([sQuery(id+"F43.wireOp",EDGE,"E102"),sQuery(id+"F43.wireOp",EDGE,"E103"),sQuery(id+"F43.wireOp",EDGE,"E104"),sQuery(id+"F43.wireOp",EDGE,"E105"),sQuery(id+"F43.wireOp",EDGE,"E106"),sQuery(id+"F43.wireOp",EDGE,"E107"),sQuery(id+"F43.wireOp",EDGE,"E108"),sQuery(id+"F43.wireOp",EDGE,"E109"),sQuery(id+"F43.wireOp",EDGE,"E110"),sQuery(id+"F43.wireOp",EDGE,"E111")])]}),"instanceName":"1"});
            var Q1;
            Q1=sQuery(id+"F0.wireOp",EDGE,"E0");
            transform(context, id + "F64", {"entities" : qUnion([Q0]), "transformType" : TransformType.ROTATION, "transformAxis" : qUnion([Q1]), "angle" : 20.77 * degree, "makeCopy" : false});
        }
        {
            var Q0;
            Q0=makeQuery(id+"F40.opExtrude","SWEPT_BODY",BODY,{"disambiguationData":[OSD([sQuery(id+"F39.wireOp",EDGE,"E92"),sQuery(id+"F39.wireOp",EDGE,"E93"),sQuery(id+"F39.wireOp",EDGE,"E94"),sQuery(id+"F39.wireOp",EDGE,"E95"),sQuery(id+"F39.wireOp",EDGE,"E96"),sQuery(id+"F39.wireOp",EDGE,"E97"),sQuery(id+"F39.wireOp",EDGE,"E98"),sQuery(id+"F39.wireOp",EDGE,"E99"),sQuery(id+"F39.wireOp",EDGE,"E100"),sQuery(id+"F39.wireOp",EDGE,"E101")])]});
            var Q1;
            Q1=qCreatedBy(id+"F58.planeOp",FACE);
            mirror(context, id + "F65", {"entities" : qUnion([Q0]), "mirrorPlane" : qUnion([Q1])});
        }
        {
            var Q0;
            Q0=makeQuery(id+"F65.opPattern","COPY",BODY,{"derivedFrom":makeQuery(id+"F40.opExtrude","SWEPT_BODY",BODY,{"disambiguationData":[OSD([sQuery(id+"F39.wireOp",EDGE,"E92"),sQuery(id+"F39.wireOp",EDGE,"E93"),sQuery(id+"F39.wireOp",EDGE,"E94"),sQuery(id+"F39.wireOp",EDGE,"E95"),sQuery(id+"F39.wireOp",EDGE,"E96"),sQuery(id+"F39.wireOp",EDGE,"E97"),sQuery(id+"F39.wireOp",EDGE,"E98"),sQuery(id+"F39.wireOp",EDGE,"E99"),sQuery(id+"F39.wireOp",EDGE,"E100"),sQuery(id+"F39.wireOp",EDGE,"E101")])]}),"instanceName":"1"});
            var Q1;
            Q1=sQuery(id+"F0.wireOp",EDGE,"E0");
            transform(context, id + "F66", {"entities" : qUnion([Q0]), "transformType" : TransformType.ROTATION, "transformAxis" : qUnion([Q1]), "angle" : 27.7 * degree, "makeCopy" : false});
        }
        {
            var Q0;
            Q0=makeQuery(id+"F36.opExtrude","SWEPT_BODY",BODY,{"disambiguationData":[OSD([sQuery(id+"F35.wireOp",EDGE,"E82"),sQuery(id+"F35.wireOp",EDGE,"E83"),sQuery(id+"F35.wireOp",EDGE,"E84"),sQuery(id+"F35.wireOp",EDGE,"E85"),sQuery(id+"F35.wireOp",EDGE,"E86"),sQuery(id+"F35.wireOp",EDGE,"E87"),sQuery(id+"F35.wireOp",EDGE,"E88"),sQuery(id+"F35.wireOp",EDGE,"E89"),sQuery(id+"F35.wireOp",EDGE,"E90"),sQuery(id+"F35.wireOp",EDGE,"E91")])]});
            var Q1;
            Q1=qCreatedBy(id+"F58.planeOp",FACE);
            mirror(context, id + "F67", {"entities" : qUnion([Q0]), "mirrorPlane" : qUnion([Q1])});
        }
        {
            var Q0;
            Q0=makeQuery(id+"F67.opPattern","COPY",BODY,{"derivedFrom":makeQuery(id+"F36.opExtrude","SWEPT_BODY",BODY,{"disambiguationData":[OSD([sQuery(id+"F35.wireOp",EDGE,"E82"),sQuery(id+"F35.wireOp",EDGE,"E83"),sQuery(id+"F35.wireOp",EDGE,"E84"),sQuery(id+"F35.wireOp",EDGE,"E85"),sQuery(id+"F35.wireOp",EDGE,"E86"),sQuery(id+"F35.wireOp",EDGE,"E87"),sQuery(id+"F35.wireOp",EDGE,"E88"),sQuery(id+"F35.wireOp",EDGE,"E89"),sQuery(id+"F35.wireOp",EDGE,"E90"),sQuery(id+"F35.wireOp",EDGE,"E91")])]}),"instanceName":"1"});
            var Q1;
            Q1=sQuery(id+"F0.wireOp",EDGE,"E0");
            transform(context, id + "F68", {"entities" : qUnion([Q0]), "transformType" : TransformType.ROTATION, "transformAxis" : qUnion([Q1]), "angle" : 34.62 * degree, "makeCopy" : false});
        }
        {
            var Q0;
            Q0=makeQuery(id+"F32.opExtrude","SWEPT_BODY",BODY,{"disambiguationData":[OSD([sQuery(id+"F31.wireOp",EDGE,"E72"),sQuery(id+"F31.wireOp",EDGE,"E73"),sQuery(id+"F31.wireOp",EDGE,"E74"),sQuery(id+"F31.wireOp",EDGE,"E75"),sQuery(id+"F31.wireOp",EDGE,"E76"),sQuery(id+"F31.wireOp",EDGE,"E77"),sQuery(id+"F31.wireOp",EDGE,"E78"),sQuery(id+"F31.wireOp",EDGE,"E79"),sQuery(id+"F31.wireOp",EDGE,"E80"),sQuery(id+"F31.wireOp",EDGE,"E81")])]});
            var Q1;
            Q1=qCreatedBy(id+"F58.planeOp",FACE);
            mirror(context, id + "F69", {"entities" : qUnion([Q0]), "mirrorPlane" : qUnion([Q1])});
        }
        {
            var Q0;
            Q0=makeQuery(id+"F69.opPattern","COPY",BODY,{"derivedFrom":makeQuery(id+"F32.opExtrude","SWEPT_BODY",BODY,{"disambiguationData":[OSD([sQuery(id+"F31.wireOp",EDGE,"E72"),sQuery(id+"F31.wireOp",EDGE,"E73"),sQuery(id+"F31.wireOp",EDGE,"E74"),sQuery(id+"F31.wireOp",EDGE,"E75"),sQuery(id+"F31.wireOp",EDGE,"E76"),sQuery(id+"F31.wireOp",EDGE,"E77"),sQuery(id+"F31.wireOp",EDGE,"E78"),sQuery(id+"F31.wireOp",EDGE,"E79"),sQuery(id+"F31.wireOp",EDGE,"E80"),sQuery(id+"F31.wireOp",EDGE,"E81")])]}),"instanceName":"1"});
            var Q1;
            Q1=sQuery(id+"F0.wireOp",EDGE,"E0");
            transform(context, id + "F70", {"entities" : qUnion([Q0]), "transformType" : TransformType.ROTATION, "transformAxis" : qUnion([Q1]), "angle" : 41.44 * degree, "makeCopy" : false});
        }
        {
            var Q0;
            Q0=makeQuery(id+"F28.opExtrude","SWEPT_BODY",BODY,{"disambiguationData":[OSD([sQuery(id+"F27.wireOp",EDGE,"E62"),sQuery(id+"F27.wireOp",EDGE,"E63"),sQuery(id+"F27.wireOp",EDGE,"E64"),sQuery(id+"F27.wireOp",EDGE,"E65"),sQuery(id+"F27.wireOp",EDGE,"E66"),sQuery(id+"F27.wireOp",EDGE,"E67"),sQuery(id+"F27.wireOp",EDGE,"E68"),sQuery(id+"F27.wireOp",EDGE,"E69"),sQuery(id+"F27.wireOp",EDGE,"E70"),sQuery(id+"F27.wireOp",EDGE,"E71")])]});
            var Q1;
            Q1=qCreatedBy(id+"F58.planeOp",FACE);
            mirror(context, id + "F71", {"entities" : qUnion([Q0]), "mirrorPlane" : qUnion([Q1])});
        }
        {
            var Q0;
            Q0=makeQuery(id+"F71.opPattern","COPY",BODY,{"derivedFrom":makeQuery(id+"F28.opExtrude","SWEPT_BODY",BODY,{"disambiguationData":[OSD([sQuery(id+"F27.wireOp",EDGE,"E62"),sQuery(id+"F27.wireOp",EDGE,"E63"),sQuery(id+"F27.wireOp",EDGE,"E64"),sQuery(id+"F27.wireOp",EDGE,"E65"),sQuery(id+"F27.wireOp",EDGE,"E66"),sQuery(id+"F27.wireOp",EDGE,"E67"),sQuery(id+"F27.wireOp",EDGE,"E68"),sQuery(id+"F27.wireOp",EDGE,"E69"),sQuery(id+"F27.wireOp",EDGE,"E70"),sQuery(id+"F27.wireOp",EDGE,"E71")])]}),"instanceName":"1"});
            var Q1;
            Q1=sQuery(id+"F0.wireOp",EDGE,"E0");
            transform(context, id + "F72", {"entities" : qUnion([Q0]), "transformType" : TransformType.ROTATION, "transformAxis" : qUnion([Q1]), "angle" : 48.46 * degree, "makeCopy" : false});
        }
        {
            var Q0;
            Q0=makeQuery(id+"F24.opExtrude","SWEPT_BODY",BODY,{"disambiguationData":[OSD([sQuery(id+"F23.wireOp",EDGE,"E52"),sQuery(id+"F23.wireOp",EDGE,"E53"),sQuery(id+"F23.wireOp",EDGE,"E54"),sQuery(id+"F23.wireOp",EDGE,"E55"),sQuery(id+"F23.wireOp",EDGE,"E56"),sQuery(id+"F23.wireOp",EDGE,"E57"),sQuery(id+"F23.wireOp",EDGE,"E58"),sQuery(id+"F23.wireOp",EDGE,"E59"),sQuery(id+"F23.wireOp",EDGE,"E60"),sQuery(id+"F23.wireOp",EDGE,"E61")])]});
            var Q1;
            Q1=qCreatedBy(id+"F58.planeOp",FACE);
            mirror(context, id + "F73", {"entities" : qUnion([Q0]), "mirrorPlane" : qUnion([Q1])});
        }
        {
            var Q0;
            Q0=makeQuery(id+"F73.opPattern","COPY",BODY,{"derivedFrom":makeQuery(id+"F24.opExtrude","SWEPT_BODY",BODY,{"disambiguationData":[OSD([sQuery(id+"F23.wireOp",EDGE,"E52"),sQuery(id+"F23.wireOp",EDGE,"E53"),sQuery(id+"F23.wireOp",EDGE,"E54"),sQuery(id+"F23.wireOp",EDGE,"E55"),sQuery(id+"F23.wireOp",EDGE,"E56"),sQuery(id+"F23.wireOp",EDGE,"E57"),sQuery(id+"F23.wireOp",EDGE,"E58"),sQuery(id+"F23.wireOp",EDGE,"E59"),sQuery(id+"F23.wireOp",EDGE,"E60"),sQuery(id+"F23.wireOp",EDGE,"E61")])]}),"instanceName":"1"});
            var Q1;
            Q1=sQuery(id+"F0.wireOp",EDGE,"E0");
            transform(context, id + "F74", {"entities" : qUnion([Q0]), "transformType" : TransformType.ROTATION, "transformAxis" : qUnion([Q1]), "angle" : 55.38 * degree, "makeCopy" : false});
        }
        {
            var Q0;
            Q0=makeQuery(id+"F20.opExtrude","SWEPT_BODY",BODY,{"disambiguationData":[OSD([sQuery(id+"F19.wireOp",EDGE,"E42"),sQuery(id+"F19.wireOp",EDGE,"E43"),sQuery(id+"F19.wireOp",EDGE,"E44"),sQuery(id+"F19.wireOp",EDGE,"E45"),sQuery(id+"F19.wireOp",EDGE,"E46"),sQuery(id+"F19.wireOp",EDGE,"E47"),sQuery(id+"F19.wireOp",EDGE,"E48"),sQuery(id+"F19.wireOp",EDGE,"E49"),sQuery(id+"F19.wireOp",EDGE,"E50"),sQuery(id+"F19.wireOp",EDGE,"E51")])]});
            var Q1;
            Q1=qCreatedBy(id+"F58.planeOp",FACE);
            mirror(context, id + "F75", {"entities" : qUnion([Q0]), "mirrorPlane" : qUnion([Q1])});
        }
        {
            var Q0;
            Q0=makeQuery(id+"F75.opPattern","COPY",BODY,{"derivedFrom":makeQuery(id+"F20.opExtrude","SWEPT_BODY",BODY,{"disambiguationData":[OSD([sQuery(id+"F19.wireOp",EDGE,"E42"),sQuery(id+"F19.wireOp",EDGE,"E43"),sQuery(id+"F19.wireOp",EDGE,"E44"),sQuery(id+"F19.wireOp",EDGE,"E45"),sQuery(id+"F19.wireOp",EDGE,"E46"),sQuery(id+"F19.wireOp",EDGE,"E47"),sQuery(id+"F19.wireOp",EDGE,"E48"),sQuery(id+"F19.wireOp",EDGE,"E49"),sQuery(id+"F19.wireOp",EDGE,"E50"),sQuery(id+"F19.wireOp",EDGE,"E51")])]}),"instanceName":"1"});
            var Q1;
            Q1=sQuery(id+"F0.wireOp",EDGE,"E0");
            transform(context, id + "F76", {"entities" : qUnion([Q0]), "transformType" : TransformType.ROTATION, "transformAxis" : qUnion([Q1]), "angle" : 62.3 * degree, "makeCopy" : false});
        }
        {
            var Q0;
            Q0=makeQuery(id+"F16.opExtrude","SWEPT_BODY",BODY,{"disambiguationData":[OSD([sQuery(id+"F15.wireOp",EDGE,"E32"),sQuery(id+"F15.wireOp",EDGE,"E33"),sQuery(id+"F15.wireOp",EDGE,"E34"),sQuery(id+"F15.wireOp",EDGE,"E35"),sQuery(id+"F15.wireOp",EDGE,"E36"),sQuery(id+"F15.wireOp",EDGE,"E37"),sQuery(id+"F15.wireOp",EDGE,"E38"),sQuery(id+"F15.wireOp",EDGE,"E39"),sQuery(id+"F15.wireOp",EDGE,"E40"),sQuery(id+"F15.wireOp",EDGE,"E41")])]});
            var Q1;
            Q1=qCreatedBy(id+"F58.planeOp",FACE);
            mirror(context, id + "F77", {"entities" : qUnion([Q0]), "mirrorPlane" : qUnion([Q1])});
        }
        {
            var Q0;
            Q0=makeQuery(id+"F77.opPattern","COPY",BODY,{"derivedFrom":makeQuery(id+"F16.opExtrude","SWEPT_BODY",BODY,{"disambiguationData":[OSD([sQuery(id+"F15.wireOp",EDGE,"E32"),sQuery(id+"F15.wireOp",EDGE,"E33"),sQuery(id+"F15.wireOp",EDGE,"E34"),sQuery(id+"F15.wireOp",EDGE,"E35"),sQuery(id+"F15.wireOp",EDGE,"E36"),sQuery(id+"F15.wireOp",EDGE,"E37"),sQuery(id+"F15.wireOp",EDGE,"E38"),sQuery(id+"F15.wireOp",EDGE,"E39"),sQuery(id+"F15.wireOp",EDGE,"E40"),sQuery(id+"F15.wireOp",EDGE,"E41")])]}),"instanceName":"1"});
            var Q1;
            Q1=sQuery(id+"F0.wireOp",EDGE,"E0");
            transform(context, id + "F78", {"entities" : qUnion([Q0]), "transformType" : TransformType.ROTATION, "transformAxis" : qUnion([Q1]), "angle" : 69.23 * degree, "makeCopy" : false});
        }
        {
            var Q0;
            Q0=makeQuery(id+"F12.opExtrude","SWEPT_BODY",BODY,{"disambiguationData":[OSD([sQuery(id+"F11.wireOp",EDGE,"E22"),sQuery(id+"F11.wireOp",EDGE,"E23"),sQuery(id+"F11.wireOp",EDGE,"E24"),sQuery(id+"F11.wireOp",EDGE,"E25"),sQuery(id+"F11.wireOp",EDGE,"E26"),sQuery(id+"F11.wireOp",EDGE,"E27"),sQuery(id+"F11.wireOp",EDGE,"E28"),sQuery(id+"F11.wireOp",EDGE,"E29"),sQuery(id+"F11.wireOp",EDGE,"E30"),sQuery(id+"F11.wireOp",EDGE,"E31")])]});
            var Q1;
            Q1=qCreatedBy(id+"F58.planeOp",FACE);
            mirror(context, id + "F79", {"entities" : qUnion([Q0]), "mirrorPlane" : qUnion([Q1])});
        }
        {
            var Q0;
            Q0=makeQuery(id+"F79.opPattern","COPY",BODY,{"derivedFrom":makeQuery(id+"F12.opExtrude","SWEPT_BODY",BODY,{"disambiguationData":[OSD([sQuery(id+"F11.wireOp",EDGE,"E22"),sQuery(id+"F11.wireOp",EDGE,"E23"),sQuery(id+"F11.wireOp",EDGE,"E24"),sQuery(id+"F11.wireOp",EDGE,"E25"),sQuery(id+"F11.wireOp",EDGE,"E26"),sQuery(id+"F11.wireOp",EDGE,"E27"),sQuery(id+"F11.wireOp",EDGE,"E28"),sQuery(id+"F11.wireOp",EDGE,"E29"),sQuery(id+"F11.wireOp",EDGE,"E30"),sQuery(id+"F11.wireOp",EDGE,"E31")])]}),"instanceName":"1"});
            var Q1;
            Q1=sQuery(id+"F0.wireOp",EDGE,"E0");
            transform(context, id + "F80", {"entities" : qUnion([Q0]), "transformType" : TransformType.ROTATION, "transformAxis" : qUnion([Q1]), "angle" : 76.15 * degree, "makeCopy" : false});
        }
        {
            var Q0;
            Q0=makeQuery(id+"F8.opExtrude","SWEPT_BODY",BODY,{"disambiguationData":[OSD([sQuery(id+"F7.wireOp",EDGE,"E12"),sQuery(id+"F7.wireOp",EDGE,"E13"),sQuery(id+"F7.wireOp",EDGE,"E14"),sQuery(id+"F7.wireOp",EDGE,"E15"),sQuery(id+"F7.wireOp",EDGE,"E16"),sQuery(id+"F7.wireOp",EDGE,"E17"),sQuery(id+"F7.wireOp",EDGE,"E18"),sQuery(id+"F7.wireOp",EDGE,"E19"),sQuery(id+"F7.wireOp",EDGE,"E20"),sQuery(id+"F7.wireOp",EDGE,"E21")])]});
            var Q1;
            Q1=qCreatedBy(id+"F58.planeOp",FACE);
            mirror(context, id + "F81", {"entities" : qUnion([Q0]), "mirrorPlane" : qUnion([Q1])});
        }
        {
            var Q0;
            Q0=makeQuery(id+"F81.opPattern","COPY",BODY,{"derivedFrom":makeQuery(id+"F8.opExtrude","SWEPT_BODY",BODY,{"disambiguationData":[OSD([sQuery(id+"F7.wireOp",EDGE,"E12"),sQuery(id+"F7.wireOp",EDGE,"E13"),sQuery(id+"F7.wireOp",EDGE,"E14"),sQuery(id+"F7.wireOp",EDGE,"E15"),sQuery(id+"F7.wireOp",EDGE,"E16"),sQuery(id+"F7.wireOp",EDGE,"E17"),sQuery(id+"F7.wireOp",EDGE,"E18"),sQuery(id+"F7.wireOp",EDGE,"E19"),sQuery(id+"F7.wireOp",EDGE,"E20"),sQuery(id+"F7.wireOp",EDGE,"E21")])]}),"instanceName":"1"});
            var Q1;
            Q1=sQuery(id+"F0.wireOp",EDGE,"E0");
            transform(context, id + "F82", {"entities" : qUnion([Q0]), "transformType" : TransformType.ROTATION, "transformAxis" : qUnion([Q1]), "angle" : 83.08 * degree, "makeCopy" : false});
        }
        {
            var Q0;
            Q0=makeQuery(id+"F4.opExtrude","SWEPT_BODY",BODY,{"disambiguationData":[OSD([sQuery(id+"F3.wireOp",EDGE,"E1"),sQuery(id+"F3.wireOp",EDGE,"E2"),sQuery(id+"F3.wireOp",EDGE,"E3"),sQuery(id+"F3.wireOp",EDGE,"E4"),sQuery(id+"F3.wireOp",EDGE,"E5"),sQuery(id+"F3.wireOp",EDGE,"E6"),sQuery(id+"F3.wireOp",EDGE,"E7"),sQuery(id+"F3.wireOp",EDGE,"E8"),sQuery(id+"F3.wireOp",EDGE,"E9"),sQuery(id+"F3.wireOp",EDGE,"E11")])]});
            var Q1;
            Q1=qCreatedBy(id+"F58.planeOp",FACE);
            mirror(context, id + "F83", {"entities" : qUnion([Q0]), "mirrorPlane" : qUnion([Q1])});
        }
        {
            var Q0;
            Q0=makeQuery(id+"F83.opPattern","COPY",BODY,{"derivedFrom":makeQuery(id+"F4.opExtrude","SWEPT_BODY",BODY,{"disambiguationData":[OSD([sQuery(id+"F3.wireOp",EDGE,"E1"),sQuery(id+"F3.wireOp",EDGE,"E2"),sQuery(id+"F3.wireOp",EDGE,"E3"),sQuery(id+"F3.wireOp",EDGE,"E4"),sQuery(id+"F3.wireOp",EDGE,"E5"),sQuery(id+"F3.wireOp",EDGE,"E6"),sQuery(id+"F3.wireOp",EDGE,"E7"),sQuery(id+"F3.wireOp",EDGE,"E8"),sQuery(id+"F3.wireOp",EDGE,"E9"),sQuery(id+"F3.wireOp",EDGE,"E11")])]}),"instanceName":"1"});
            var Q1;
            Q1=sQuery(id+"F0.wireOp",EDGE,"E0");
            transform(context, id + "F84", {"entities" : qUnion([Q0]), "transformType" : TransformType.ROTATION, "transformAxis" : qUnion([Q1]), "angle" : 90 * degree, "makeCopy" : false});
        }
        {
            var Q0;
            Q0=makeQuery(id+"F8.opExtrude","CAP_FACE",FACE,{"disambiguationData":[OSD([sQuery(id+"F7.wireOp",EDGE,"E12"),sQuery(id+"F7.wireOp",EDGE,"E13"),sQuery(id+"F7.wireOp",EDGE,"E14"),sQuery(id+"F7.wireOp",EDGE,"E15"),sQuery(id+"F7.wireOp",EDGE,"E16"),sQuery(id+"F7.wireOp",EDGE,"E17"),sQuery(id+"F7.wireOp",EDGE,"E18"),sQuery(id+"F7.wireOp",EDGE,"E19"),sQuery(id+"F7.wireOp",EDGE,"E20"),sQuery(id+"F7.wireOp",EDGE,"E21")])],"isStart":true});
            var sketch = newSketch(context, id + "F85", { "sketchPlane" : qUnion([Q0])});
            skCircle(sketch, "E142.0", {"center": v(23.5, -59.5) * mm, "radius": 2.35 * mm});
            skCircle(sketch, "E143.0", {"center": v(-23.5, 59.5) * mm, "radius": 2.35 * mm});
            skSolve(sketch);
        }
        {
            var Q0;
            Q0 = qSketchRegion(id + "F85", true);
            extrude(context, id + "F86", {"entities" : qUnion([Q0]), "operationType" : NewBodyOperationType.REMOVE, "oppositeDirection" : true, "depth" : (getVariable(context, 'thick')) * mm});
        }
        {
            var Q0;
            Q0=makeQuery(id+"F12.opExtrude","CAP_FACE",FACE,{"disambiguationData":[OSD([sQuery(id+"F11.wireOp",EDGE,"E22"),sQuery(id+"F11.wireOp",EDGE,"E23"),sQuery(id+"F11.wireOp",EDGE,"E24"),sQuery(id+"F11.wireOp",EDGE,"E25"),sQuery(id+"F11.wireOp",EDGE,"E26"),sQuery(id+"F11.wireOp",EDGE,"E27"),sQuery(id+"F11.wireOp",EDGE,"E28"),sQuery(id+"F11.wireOp",EDGE,"E29"),sQuery(id+"F11.wireOp",EDGE,"E30"),sQuery(id+"F11.wireOp",EDGE,"E31")])],"isStart":true});
            var sketch = newSketch(context, id + "F87", { "sketchPlane" : qUnion([Q0])});
            skCircle(sketch, "E144.0", {"center": v(-33.8, 63.92) * mm, "radius": 2.35 * mm});
            skCircle(sketch, "E145.0", {"center": v(33.8, -63.92) * mm, "radius": 2.35 * mm});
            skSolve(sketch);
        }
        {
            var Q0;
            Q0 = qSketchRegion(id + "F87", true);
            extrude(context, id + "F88", {"entities" : qUnion([Q0]), "operationType" : NewBodyOperationType.REMOVE, "oppositeDirection" : true, "depth" : (getVariable(context, 'thick')) * mm});
        }
        {
            var Q0;
            Q0=makeQuery(id+"F16.opExtrude","CAP_FACE",FACE,{"disambiguationData":[OSD([sQuery(id+"F15.wireOp",EDGE,"E32"),sQuery(id+"F15.wireOp",EDGE,"E33"),sQuery(id+"F15.wireOp",EDGE,"E34"),sQuery(id+"F15.wireOp",EDGE,"E35"),sQuery(id+"F15.wireOp",EDGE,"E36"),sQuery(id+"F15.wireOp",EDGE,"E37"),sQuery(id+"F15.wireOp",EDGE,"E38"),sQuery(id+"F15.wireOp",EDGE,"E39"),sQuery(id+"F15.wireOp",EDGE,"E40"),sQuery(id+"F15.wireOp",EDGE,"E41")])],"isStart":true});
            var sketch = newSketch(context, id + "F89", { "sketchPlane" : qUnion([Q0])});
            skCircle(sketch, "E146.0", {"center": v(-44.7, 67.3) * mm, "radius": 2.35 * mm});
            skCircle(sketch, "E147.0", {"center": v(44.7, -67.3) * mm, "radius": 2.35 * mm});
            skSolve(sketch);
        }
        {
            var Q0;
            Q0 = qSketchRegion(id + "F89", true);
            extrude(context, id + "F90", {"entities" : qUnion([Q0]), "operationType" : NewBodyOperationType.REMOVE, "oppositeDirection" : true, "depth" : (getVariable(context, 'thick')) * mm});
        }
        {
            var Q0;
            Q0=makeQuery(id+"F20.opExtrude","CAP_FACE",FACE,{"disambiguationData":[OSD([sQuery(id+"F19.wireOp",EDGE,"E42"),sQuery(id+"F19.wireOp",EDGE,"E43"),sQuery(id+"F19.wireOp",EDGE,"E44"),sQuery(id+"F19.wireOp",EDGE,"E45"),sQuery(id+"F19.wireOp",EDGE,"E46"),sQuery(id+"F19.wireOp",EDGE,"E47"),sQuery(id+"F19.wireOp",EDGE,"E48"),sQuery(id+"F19.wireOp",EDGE,"E49"),sQuery(id+"F19.wireOp",EDGE,"E50"),sQuery(id+"F19.wireOp",EDGE,"E51")])],"isStart":true});
            var sketch = newSketch(context, id + "F91", { "sketchPlane" : qUnion([Q0])});
            skCircle(sketch, "E148.0", {"center": v(-56.1, 69.57) * mm, "radius": 2.35 * mm});
            skCircle(sketch, "E149.0", {"center": v(56.1, -69.57) * mm, "radius": 2.35 * mm});
            skSolve(sketch);
        }
        {
            var Q0;
            Q0 = qSketchRegion(id + "F91", true);
            extrude(context, id + "F92", {"entities" : qUnion([Q0]), "operationType" : NewBodyOperationType.REMOVE, "oppositeDirection" : true, "depth" : (getVariable(context, 'thick')) * mm});
        }
        {
            var Q0;
            Q0=makeQuery(id+"F24.opExtrude","CAP_FACE",FACE,{"disambiguationData":[OSD([sQuery(id+"F23.wireOp",EDGE,"E52"),sQuery(id+"F23.wireOp",EDGE,"E53"),sQuery(id+"F23.wireOp",EDGE,"E54"),sQuery(id+"F23.wireOp",EDGE,"E55"),sQuery(id+"F23.wireOp",EDGE,"E56"),sQuery(id+"F23.wireOp",EDGE,"E57"),sQuery(id+"F23.wireOp",EDGE,"E58"),sQuery(id+"F23.wireOp",EDGE,"E59"),sQuery(id+"F23.wireOp",EDGE,"E60"),sQuery(id+"F23.wireOp",EDGE,"E61")])],"isStart":true});
            var sketch = newSketch(context, id + "F93", { "sketchPlane" : qUnion([Q0])});
            skCircle(sketch, "E150.0", {"center": v(67.9, -70.7) * mm, "radius": 2.35 * mm});
            skCircle(sketch, "E151.0", {"center": v(-67.9, 70.7) * mm, "radius": 2.35 * mm});
            skSolve(sketch);
        }
        {
            var Q0;
            Q0 = qSketchRegion(id + "F93", true);
            extrude(context, id + "F94", {"entities" : qUnion([Q0]), "operationType" : NewBodyOperationType.REMOVE, "oppositeDirection" : true, "depth" : (getVariable(context, 'thick')) * mm});
        }
        {
            var Q0;
            Q0=makeQuery(id+"F28.opExtrude","CAP_FACE",FACE,{"disambiguationData":[OSD([sQuery(id+"F27.wireOp",EDGE,"E62"),sQuery(id+"F27.wireOp",EDGE,"E63"),sQuery(id+"F27.wireOp",EDGE,"E64"),sQuery(id+"F27.wireOp",EDGE,"E65"),sQuery(id+"F27.wireOp",EDGE,"E66"),sQuery(id+"F27.wireOp",EDGE,"E67"),sQuery(id+"F27.wireOp",EDGE,"E68"),sQuery(id+"F27.wireOp",EDGE,"E69"),sQuery(id+"F27.wireOp",EDGE,"E70"),sQuery(id+"F27.wireOp",EDGE,"E71")])],"isStart":true});
            var sketch = newSketch(context, id + "F95", { "sketchPlane" : qUnion([Q0])});
            skCircle(sketch, "E152.0", {"center": v(-80.02, 70.63) * mm, "radius": 2.35 * mm});
            skCircle(sketch, "E153.0", {"center": v(80.02, -70.63) * mm, "radius": 2.35 * mm});
            skSolve(sketch);
        }
        {
            var Q0;
            Q0 = qSketchRegion(id + "F95", true);
            extrude(context, id + "F96", {"entities" : qUnion([Q0]), "operationType" : NewBodyOperationType.REMOVE, "oppositeDirection" : true, "depth" : (getVariable(context, 'thick')) * mm});
        }
        {
            var Q0;
            Q0=makeQuery(id+"F32.opExtrude","CAP_FACE",FACE,{"disambiguationData":[OSD([sQuery(id+"F31.wireOp",EDGE,"E72"),sQuery(id+"F31.wireOp",EDGE,"E73"),sQuery(id+"F31.wireOp",EDGE,"E74"),sQuery(id+"F31.wireOp",EDGE,"E75"),sQuery(id+"F31.wireOp",EDGE,"E76"),sQuery(id+"F31.wireOp",EDGE,"E77"),sQuery(id+"F31.wireOp",EDGE,"E78"),sQuery(id+"F31.wireOp",EDGE,"E79"),sQuery(id+"F31.wireOp",EDGE,"E80"),sQuery(id+"F31.wireOp",EDGE,"E81")])],"isStart":true});
            var sketch = newSketch(context, id + "F97", { "sketchPlane" : qUnion([Q0])});
            skCircle(sketch, "E154.0", {"center": v(92.35, -69.34) * mm, "radius": 2.35 * mm});
            skCircle(sketch, "E155.0", {"center": v(-92.35, 69.34) * mm, "radius": 2.35 * mm});
            skSolve(sketch);
        }
        {
            var Q0;
            Q0 = qSketchRegion(id + "F97", true);
            extrude(context, id + "F98", {"entities" : qUnion([Q0]), "operationType" : NewBodyOperationType.REMOVE, "oppositeDirection" : true, "depth" : (getVariable(context, 'thick')) * mm});
        }
        {
            var Q0;
            Q0=makeQuery(id+"F36.opExtrude","CAP_FACE",FACE,{"disambiguationData":[OSD([sQuery(id+"F35.wireOp",EDGE,"E82"),sQuery(id+"F35.wireOp",EDGE,"E83"),sQuery(id+"F35.wireOp",EDGE,"E84"),sQuery(id+"F35.wireOp",EDGE,"E85"),sQuery(id+"F35.wireOp",EDGE,"E86"),sQuery(id+"F35.wireOp",EDGE,"E87"),sQuery(id+"F35.wireOp",EDGE,"E88"),sQuery(id+"F35.wireOp",EDGE,"E89"),sQuery(id+"F35.wireOp",EDGE,"E90"),sQuery(id+"F35.wireOp",EDGE,"E91")])],"isStart":true});
            var sketch = newSketch(context, id + "F99", { "sketchPlane" : qUnion([Q0])});
            skCircle(sketch, "E156.0", {"center": v(-104.8, 66.81) * mm, "radius": 2.35 * mm});
            skCircle(sketch, "E157.0", {"center": v(104.8, -66.81) * mm, "radius": 2.35 * mm});
            skSolve(sketch);
        }
        {
            var Q0;
            Q0 = qSketchRegion(id + "F99", true);
            extrude(context, id + "F100", {"entities" : qUnion([Q0]), "operationType" : NewBodyOperationType.REMOVE, "oppositeDirection" : true, "depth" : (getVariable(context, 'thick')) * mm});
        }
        {
            var Q0;
            Q0=makeQuery(id+"F40.opExtrude","CAP_FACE",FACE,{"disambiguationData":[OSD([sQuery(id+"F39.wireOp",EDGE,"E92"),sQuery(id+"F39.wireOp",EDGE,"E93"),sQuery(id+"F39.wireOp",EDGE,"E94"),sQuery(id+"F39.wireOp",EDGE,"E95"),sQuery(id+"F39.wireOp",EDGE,"E96"),sQuery(id+"F39.wireOp",EDGE,"E97"),sQuery(id+"F39.wireOp",EDGE,"E98"),sQuery(id+"F39.wireOp",EDGE,"E99"),sQuery(id+"F39.wireOp",EDGE,"E100"),sQuery(id+"F39.wireOp",EDGE,"E101")])],"isStart":true});
            var sketch = newSketch(context, id + "F101", { "sketchPlane" : qUnion([Q0])});
            skCircle(sketch, "E158.0", {"center": v(117.23, -63.02) * mm, "radius": 2.35 * mm});
            skCircle(sketch, "E159.0", {"center": v(-117.23, 63.02) * mm, "radius": 2.35 * mm});
            skSolve(sketch);
        }
        {
            var Q0;
            Q0 = qSketchRegion(id + "F101", true);
            extrude(context, id + "F102", {"entities" : qUnion([Q0]), "operationType" : NewBodyOperationType.REMOVE, "oppositeDirection" : true, "depth" : (getVariable(context, 'thick')) * mm});
        }
        {
            var Q0;
            Q0=makeQuery(id+"F44.opExtrude","CAP_FACE",FACE,{"disambiguationData":[OSD([sQuery(id+"F43.wireOp",EDGE,"E102"),sQuery(id+"F43.wireOp",EDGE,"E103"),sQuery(id+"F43.wireOp",EDGE,"E104"),sQuery(id+"F43.wireOp",EDGE,"E105"),sQuery(id+"F43.wireOp",EDGE,"E106"),sQuery(id+"F43.wireOp",EDGE,"E107"),sQuery(id+"F43.wireOp",EDGE,"E108"),sQuery(id+"F43.wireOp",EDGE,"E109"),sQuery(id+"F43.wireOp",EDGE,"E110"),sQuery(id+"F43.wireOp",EDGE,"E111")])],"isStart":true});
            var sketch = newSketch(context, id + "F103", { "sketchPlane" : qUnion([Q0])});
            skCircle(sketch, "E160.0", {"center": v(-129.57, 57.97) * mm, "radius": 2.35 * mm});
            skCircle(sketch, "E161.0", {"center": v(129.57, -57.97) * mm, "radius": 2.35 * mm});
            skSolve(sketch);
        }
        {
            var Q0;
            Q0 = qSketchRegion(id + "F103", true);
            extrude(context, id + "F104", {"entities" : qUnion([Q0]), "operationType" : NewBodyOperationType.REMOVE, "oppositeDirection" : true, "depth" : (getVariable(context, 'thick')) * mm});
        }
        {
            var Q0;
            Q0=makeQuery(id+"F48.opExtrude","CAP_FACE",FACE,{"disambiguationData":[OSD([sQuery(id+"F47.wireOp",EDGE,"E112"),sQuery(id+"F47.wireOp",EDGE,"E113"),sQuery(id+"F47.wireOp",EDGE,"E114"),sQuery(id+"F47.wireOp",EDGE,"E115"),sQuery(id+"F47.wireOp",EDGE,"E116"),sQuery(id+"F47.wireOp",EDGE,"E117"),sQuery(id+"F47.wireOp",EDGE,"E118"),sQuery(id+"F47.wireOp",EDGE,"E119"),sQuery(id+"F47.wireOp",EDGE,"E120"),sQuery(id+"F47.wireOp",EDGE,"E121")])],"isStart":true});
            var sketch = newSketch(context, id + "F105", { "sketchPlane" : qUnion([Q0])});
            skCircle(sketch, "E162.0", {"center": v(141.68, -51.64) * mm, "radius": 2.35 * mm});
            skCircle(sketch, "E163.0", {"center": v(-141.68, 51.64) * mm, "radius": 2.35 * mm});
            skSolve(sketch);
        }
        {
            var Q0;
            Q0 = qSketchRegion(id + "F105", true);
            extrude(context, id + "F106", {"entities" : qUnion([Q0]), "operationType" : NewBodyOperationType.REMOVE, "oppositeDirection" : true, "depth" : (getVariable(context, 'thick')) * mm});
        }
        {
            var Q0;
            Q0=makeQuery(id+"F52.opExtrude","CAP_FACE",FACE,{"disambiguationData":[OSD([sQuery(id+"F51.wireOp",EDGE,"E122"),sQuery(id+"F51.wireOp",EDGE,"E123"),sQuery(id+"F51.wireOp",EDGE,"E124"),sQuery(id+"F51.wireOp",EDGE,"E125"),sQuery(id+"F51.wireOp",EDGE,"E126"),sQuery(id+"F51.wireOp",EDGE,"E127"),sQuery(id+"F51.wireOp",EDGE,"E128"),sQuery(id+"F51.wireOp",EDGE,"E129"),sQuery(id+"F51.wireOp",EDGE,"E130"),sQuery(id+"F51.wireOp",EDGE,"E131")])],"isStart":true});
            var sketch = newSketch(context, id + "F107", { "sketchPlane" : qUnion([Q0])});
            skCircle(sketch, "E164.0", {"center": v(-153.48, 44.06) * mm, "radius": 2.35 * mm});
            skCircle(sketch, "E165.0", {"center": v(153.48, -44.06) * mm, "radius": 2.35 * mm});
            skSolve(sketch);
        }
        {
            var Q0;
            Q0 = qSketchRegion(id + "F107", true);
            extrude(context, id + "F108", {"entities" : qUnion([Q0]), "operationType" : NewBodyOperationType.REMOVE, "oppositeDirection" : true, "depth" : (getVariable(context, 'thick')) * mm});
        }
        {
            var Q0;
            Q0=makeQuery(id+"F56.opExtrude","CAP_FACE",FACE,{"disambiguationData":[OSD([sQuery(id+"F55.wireOp",EDGE,"E132"),sQuery(id+"F55.wireOp",EDGE,"E133"),sQuery(id+"F55.wireOp",EDGE,"E134"),sQuery(id+"F55.wireOp",EDGE,"E135"),sQuery(id+"F55.wireOp",EDGE,"E136"),sQuery(id+"F55.wireOp",EDGE,"E137"),sQuery(id+"F55.wireOp",EDGE,"E138"),sQuery(id+"F55.wireOp",EDGE,"E139"),sQuery(id+"F55.wireOp",EDGE,"E140"),sQuery(id+"F55.wireOp",EDGE,"E141")])],"isStart":true});
            var sketch = newSketch(context, id + "F109", { "sketchPlane" : qUnion([Q0])});
            skCircle(sketch, "E166.0", {"center": v(164.84, -35.24) * mm, "radius": 2.35 * mm});
            skCircle(sketch, "E167.0", {"center": v(-164.84, 35.24) * mm, "radius": 2.35 * mm});
            skSolve(sketch);
        }
        {
            var Q0;
            Q0 = qSketchRegion(id + "F109", true);
            extrude(context, id + "F110", {"entities" : qUnion([Q0]), "operationType" : NewBodyOperationType.REMOVE, "oppositeDirection" : true, "depth" : (getVariable(context, 'thick')) * mm});
        }
        {
            var Q0;
            Q0=makeQuery(id+"F56.opExtrude","CAP_FACE",FACE,{"disambiguationData":[OSD([sQuery(id+"F55.wireOp",EDGE,"E132"),sQuery(id+"F55.wireOp",EDGE,"E133"),sQuery(id+"F55.wireOp",EDGE,"E134"),sQuery(id+"F55.wireOp",EDGE,"E135"),sQuery(id+"F55.wireOp",EDGE,"E136"),sQuery(id+"F55.wireOp",EDGE,"E137"),sQuery(id+"F55.wireOp",EDGE,"E138"),sQuery(id+"F55.wireOp",EDGE,"E139"),sQuery(id+"F55.wireOp",EDGE,"E140"),sQuery(id+"F55.wireOp",EDGE,"E141")])],"isStart":false});
            var sketch = newSketch(context, id + "F111", { "sketchPlane" : qUnion([Q0])});
            skCircle(sketch, "E168.0", {"center": v(167.88, 15.12) * mm, "radius": 2.35 * mm});
            skCircle(sketch, "E169.0", {"center": v(-167.88, -15.12) * mm, "radius": 2.35 * mm});
            skSolve(sketch);
        }
        {
            var Q0;
            Q0 = qSketchRegion(id + "F111", true);
            extrude(context, id + "F112", {"entities" : qUnion([Q0]), "operationType" : NewBodyOperationType.REMOVE, "oppositeDirection" : true, "depth" : (getVariable(context, 'thick')) * mm});
        }
        {
            var Q0;
            Q0=makeQuery(id+"F59.opPattern","COPY",FACE,{"derivedFrom":makeQuery(id+"F52.opExtrude","CAP_FACE",FACE,{"disambiguationData":[OSD([sQuery(id+"F51.wireOp",EDGE,"E122"),sQuery(id+"F51.wireOp",EDGE,"E123"),sQuery(id+"F51.wireOp",EDGE,"E124"),sQuery(id+"F51.wireOp",EDGE,"E125"),sQuery(id+"F51.wireOp",EDGE,"E126"),sQuery(id+"F51.wireOp",EDGE,"E127"),sQuery(id+"F51.wireOp",EDGE,"E128"),sQuery(id+"F51.wireOp",EDGE,"E129"),sQuery(id+"F51.wireOp",EDGE,"E130"),sQuery(id+"F51.wireOp",EDGE,"E131")])],"isStart":true}),"instanceName":"1"});
            var sketch = newSketch(context, id + "F113", { "sketchPlane" : qUnion([Q0])});
            skCircle(sketch, "E170.0", {"center": v(159.56, 6.05) * mm, "radius": 2.35 * mm});
            skCircle(sketch, "E171.0", {"center": v(-159.56, -6.05) * mm, "radius": 2.35 * mm});
            skSolve(sketch);
        }
        {
            var Q0;
            Q0 = qSketchRegion(id + "F113", true);
            extrude(context, id + "F114", {"entities" : qUnion([Q0]), "operationType" : NewBodyOperationType.REMOVE, "oppositeDirection" : true, "depth" : (getVariable(context, 'thick')) * mm});
        }
        {
            var Q0;
            Q0=makeQuery(id+"F61.opPattern","COPY",FACE,{"derivedFrom":makeQuery(id+"F48.opExtrude","CAP_FACE",FACE,{"disambiguationData":[OSD([sQuery(id+"F47.wireOp",EDGE,"E112"),sQuery(id+"F47.wireOp",EDGE,"E113"),sQuery(id+"F47.wireOp",EDGE,"E114"),sQuery(id+"F47.wireOp",EDGE,"E115"),sQuery(id+"F47.wireOp",EDGE,"E116"),sQuery(id+"F47.wireOp",EDGE,"E117"),sQuery(id+"F47.wireOp",EDGE,"E118"),sQuery(id+"F47.wireOp",EDGE,"E119"),sQuery(id+"F47.wireOp",EDGE,"E120"),sQuery(id+"F47.wireOp",EDGE,"E121")])],"isStart":true}),"instanceName":"1"});
            var sketch = newSketch(context, id + "F115", { "sketchPlane" : qUnion([Q0])});
            skCircle(sketch, "E172.0", {"center": v(-150.79, 1.96) * mm, "radius": 2.35 * mm});
            skCircle(sketch, "E173.0", {"center": v(150.79, -1.96) * mm, "radius": 2.35 * mm});
            skSolve(sketch);
        }
        {
            var Q0;
            Q0 = qSketchRegion(id + "F115", true);
            extrude(context, id + "F116", {"entities" : qUnion([Q0]), "operationType" : NewBodyOperationType.REMOVE, "oppositeDirection" : true, "depth" : (getVariable(context, 'thick')) * mm});
        }
        {
            var Q0;
            Q0=makeQuery(id+"F63.opPattern","COPY",FACE,{"derivedFrom":makeQuery(id+"F44.opExtrude","CAP_FACE",FACE,{"disambiguationData":[OSD([sQuery(id+"F43.wireOp",EDGE,"E102"),sQuery(id+"F43.wireOp",EDGE,"E103"),sQuery(id+"F43.wireOp",EDGE,"E104"),sQuery(id+"F43.wireOp",EDGE,"E105"),sQuery(id+"F43.wireOp",EDGE,"E106"),sQuery(id+"F43.wireOp",EDGE,"E107"),sQuery(id+"F43.wireOp",EDGE,"E108"),sQuery(id+"F43.wireOp",EDGE,"E109"),sQuery(id+"F43.wireOp",EDGE,"E110"),sQuery(id+"F43.wireOp",EDGE,"E111")])],"isStart":true}),"instanceName":"1"});
            var sketch = newSketch(context, id + "F117", { "sketchPlane" : qUnion([Q0])});
            skCircle(sketch, "E174.0", {"center": v(141.66, -8.89) * mm, "radius": 2.35 * mm});
            skCircle(sketch, "E175.0", {"center": v(-141.66, 8.89) * mm, "radius": 2.35 * mm});
            skSolve(sketch);
        }
        {
            var Q0;
            Q0 = qSketchRegion(id + "F117", true);
            extrude(context, id + "F118", {"entities" : qUnion([Q0]), "operationType" : NewBodyOperationType.REMOVE, "oppositeDirection" : true, "depth" : (getVariable(context, 'thick')) * mm});
        }
        {
            var Q0;
            Q0=makeQuery(id+"F65.opPattern","COPY",FACE,{"derivedFrom":makeQuery(id+"F40.opExtrude","CAP_FACE",FACE,{"disambiguationData":[OSD([sQuery(id+"F39.wireOp",EDGE,"E92"),sQuery(id+"F39.wireOp",EDGE,"E93"),sQuery(id+"F39.wireOp",EDGE,"E94"),sQuery(id+"F39.wireOp",EDGE,"E95"),sQuery(id+"F39.wireOp",EDGE,"E96"),sQuery(id+"F39.wireOp",EDGE,"E97"),sQuery(id+"F39.wireOp",EDGE,"E98"),sQuery(id+"F39.wireOp",EDGE,"E99"),sQuery(id+"F39.wireOp",EDGE,"E100"),sQuery(id+"F39.wireOp",EDGE,"E101")])],"isStart":true}),"instanceName":"1"});
            var sketch = newSketch(context, id + "F119", { "sketchPlane" : qUnion([Q0])});
            skCircle(sketch, "E176.0", {"center": v(-132.28, 14.73) * mm, "radius": 2.35 * mm});
            skCircle(sketch, "E177.0", {"center": v(132.28, -14.73) * mm, "radius": 2.35 * mm});
            skSolve(sketch);
        }
        {
            var Q0;
            Q0 = qSketchRegion(id + "F119", true);
            extrude(context, id + "F120", {"entities" : qUnion([Q0]), "operationType" : NewBodyOperationType.REMOVE, "oppositeDirection" : true, "depth" : (getVariable(context, 'thick')) * mm});
        }
        {
            var Q0;
            Q0=makeQuery(id+"F67.opPattern","COPY",FACE,{"derivedFrom":makeQuery(id+"F36.opExtrude","CAP_FACE",FACE,{"disambiguationData":[OSD([sQuery(id+"F35.wireOp",EDGE,"E82"),sQuery(id+"F35.wireOp",EDGE,"E83"),sQuery(id+"F35.wireOp",EDGE,"E84"),sQuery(id+"F35.wireOp",EDGE,"E85"),sQuery(id+"F35.wireOp",EDGE,"E86"),sQuery(id+"F35.wireOp",EDGE,"E87"),sQuery(id+"F35.wireOp",EDGE,"E88"),sQuery(id+"F35.wireOp",EDGE,"E89"),sQuery(id+"F35.wireOp",EDGE,"E90"),sQuery(id+"F35.wireOp",EDGE,"E91")])],"isStart":true}),"instanceName":"1"});
            var sketch = newSketch(context, id + "F121", { "sketchPlane" : qUnion([Q0])});
            skCircle(sketch, "E178.0", {"center": v(122.78, -19.27) * mm, "radius": 2.35 * mm});
            skCircle(sketch, "E179.0", {"center": v(-122.78, 19.27) * mm, "radius": 2.35 * mm});
            skSolve(sketch);
        }
        {
            var Q0;
            Q0 = qSketchRegion(id + "F121", true);
            extrude(context, id + "F122", {"entities" : qUnion([Q0]), "operationType" : NewBodyOperationType.REMOVE, "oppositeDirection" : true, "depth" : (getVariable(context, 'thick')) * mm});
        }
        {
            var Q0;
            Q0=makeQuery(id+"F69.opPattern","COPY",FACE,{"derivedFrom":makeQuery(id+"F32.opExtrude","CAP_FACE",FACE,{"disambiguationData":[OSD([sQuery(id+"F31.wireOp",EDGE,"E72"),sQuery(id+"F31.wireOp",EDGE,"E73"),sQuery(id+"F31.wireOp",EDGE,"E74"),sQuery(id+"F31.wireOp",EDGE,"E75"),sQuery(id+"F31.wireOp",EDGE,"E76"),sQuery(id+"F31.wireOp",EDGE,"E77"),sQuery(id+"F31.wireOp",EDGE,"E78"),sQuery(id+"F31.wireOp",EDGE,"E79"),sQuery(id+"F31.wireOp",EDGE,"E80"),sQuery(id+"F31.wireOp",EDGE,"E81")])],"isStart":true}),"instanceName":"1"});
            var sketch = newSketch(context, id + "F123", { "sketchPlane" : qUnion([Q0])});
            skCircle(sketch, "E180.0", {"center": v(-113.15, 23.15) * mm, "radius": 2.35 * mm});
            skCircle(sketch, "E181.0", {"center": v(113.15, -23.15) * mm, "radius": 2.35 * mm});
            skSolve(sketch);
        }
        {
            var Q0;
            Q0 = qSketchRegion(id + "F123", true);
            extrude(context, id + "F124", {"entities" : qUnion([Q0]), "operationType" : NewBodyOperationType.REMOVE, "oppositeDirection" : true, "depth" : (getVariable(context, 'thick')) * mm});
        }
        {
            var Q0;
            Q0=makeQuery(id+"F71.opPattern","COPY",FACE,{"derivedFrom":makeQuery(id+"F28.opExtrude","CAP_FACE",FACE,{"disambiguationData":[OSD([sQuery(id+"F27.wireOp",EDGE,"E62"),sQuery(id+"F27.wireOp",EDGE,"E63"),sQuery(id+"F27.wireOp",EDGE,"E64"),sQuery(id+"F27.wireOp",EDGE,"E65"),sQuery(id+"F27.wireOp",EDGE,"E66"),sQuery(id+"F27.wireOp",EDGE,"E67"),sQuery(id+"F27.wireOp",EDGE,"E68"),sQuery(id+"F27.wireOp",EDGE,"E69"),sQuery(id+"F27.wireOp",EDGE,"E70"),sQuery(id+"F27.wireOp",EDGE,"E71")])],"isStart":true}),"instanceName":"1"});
            var sketch = newSketch(context, id + "F125", { "sketchPlane" : qUnion([Q0])});
            skCircle(sketch, "E182.0", {"center": v(103.58, -25.74) * mm, "radius": 2.35 * mm});
            skCircle(sketch, "E183.0", {"center": v(-103.58, 25.74) * mm, "radius": 2.35 * mm});
            skSolve(sketch);
        }
        {
            var Q0;
            Q0 = qSketchRegion(id + "F125", true);
            extrude(context, id + "F126", {"entities" : qUnion([Q0]), "operationType" : NewBodyOperationType.REMOVE, "oppositeDirection" : true, "depth" : (getVariable(context, 'thick')) * mm});
        }
        {
            var Q0;
            Q0=makeQuery(id+"F73.opPattern","COPY",FACE,{"derivedFrom":makeQuery(id+"F24.opExtrude","CAP_FACE",FACE,{"disambiguationData":[OSD([sQuery(id+"F23.wireOp",EDGE,"E52"),sQuery(id+"F23.wireOp",EDGE,"E53"),sQuery(id+"F23.wireOp",EDGE,"E54"),sQuery(id+"F23.wireOp",EDGE,"E55"),sQuery(id+"F23.wireOp",EDGE,"E56"),sQuery(id+"F23.wireOp",EDGE,"E57"),sQuery(id+"F23.wireOp",EDGE,"E58"),sQuery(id+"F23.wireOp",EDGE,"E59"),sQuery(id+"F23.wireOp",EDGE,"E60"),sQuery(id+"F23.wireOp",EDGE,"E61")])],"isStart":true}),"instanceName":"1"});
            var sketch = newSketch(context, id + "F127", { "sketchPlane" : qUnion([Q0])});
            skCircle(sketch, "E184.0", {"center": v(-94.15, 27.27) * mm, "radius": 2.35 * mm});
            skCircle(sketch, "E185.0", {"center": v(94.15, -27.27) * mm, "radius": 2.35 * mm});
            skSolve(sketch);
        }
        {
            var Q0;
            Q0 = qSketchRegion(id + "F127", true);
            extrude(context, id + "F128", {"entities" : qUnion([Q0]), "operationType" : NewBodyOperationType.REMOVE, "oppositeDirection" : true, "depth" : (getVariable(context, 'thick')) * mm});
        }
        {
            var Q0;
            Q0=makeQuery(id+"F75.opPattern","COPY",FACE,{"derivedFrom":makeQuery(id+"F20.opExtrude","CAP_FACE",FACE,{"disambiguationData":[OSD([sQuery(id+"F19.wireOp",EDGE,"E42"),sQuery(id+"F19.wireOp",EDGE,"E43"),sQuery(id+"F19.wireOp",EDGE,"E44"),sQuery(id+"F19.wireOp",EDGE,"E45"),sQuery(id+"F19.wireOp",EDGE,"E46"),sQuery(id+"F19.wireOp",EDGE,"E47"),sQuery(id+"F19.wireOp",EDGE,"E48"),sQuery(id+"F19.wireOp",EDGE,"E49"),sQuery(id+"F19.wireOp",EDGE,"E50"),sQuery(id+"F19.wireOp",EDGE,"E51")])],"isStart":true}),"instanceName":"1"});
            var sketch = newSketch(context, id + "F129", { "sketchPlane" : qUnion([Q0])});
            skCircle(sketch, "E186.0", {"center": v(84.94, -27.78) * mm, "radius": 2.35 * mm});
            skCircle(sketch, "E187.0", {"center": v(-84.94, 27.78) * mm, "radius": 2.35 * mm});
            skSolve(sketch);
        }
        {
            var Q0;
            Q0 = qSketchRegion(id + "F129", true);
            extrude(context, id + "F130", {"entities" : qUnion([Q0]), "operationType" : NewBodyOperationType.REMOVE, "oppositeDirection" : true, "depth" : (getVariable(context, 'thick')) * mm});
        }
        {
            var Q0;
            Q0=makeQuery(id+"F77.opPattern","COPY",FACE,{"derivedFrom":makeQuery(id+"F16.opExtrude","CAP_FACE",FACE,{"disambiguationData":[OSD([sQuery(id+"F15.wireOp",EDGE,"E32"),sQuery(id+"F15.wireOp",EDGE,"E33"),sQuery(id+"F15.wireOp",EDGE,"E34"),sQuery(id+"F15.wireOp",EDGE,"E35"),sQuery(id+"F15.wireOp",EDGE,"E36"),sQuery(id+"F15.wireOp",EDGE,"E37"),sQuery(id+"F15.wireOp",EDGE,"E38"),sQuery(id+"F15.wireOp",EDGE,"E39"),sQuery(id+"F15.wireOp",EDGE,"E40"),sQuery(id+"F15.wireOp",EDGE,"E41")])],"isStart":true}),"instanceName":"1"});
            var sketch = newSketch(context, id + "F131", { "sketchPlane" : qUnion([Q0])});
            skCircle(sketch, "E188.0", {"center": v(-76.04, 27.29) * mm, "radius": 2.35 * mm});
            skCircle(sketch, "E189.0", {"center": v(76.04, -27.29) * mm, "radius": 2.35 * mm});
            skSolve(sketch);
        }
        {
            var Q0;
            Q0 = qSketchRegion(id + "F131", true);
            extrude(context, id + "F132", {"entities" : qUnion([Q0]), "operationType" : NewBodyOperationType.REMOVE, "oppositeDirection" : true, "depth" : (getVariable(context, 'thick')) * mm});
        }
        {
            var Q0;
            Q0=makeQuery(id+"F79.opPattern","COPY",FACE,{"derivedFrom":makeQuery(id+"F12.opExtrude","CAP_FACE",FACE,{"disambiguationData":[OSD([sQuery(id+"F11.wireOp",EDGE,"E22"),sQuery(id+"F11.wireOp",EDGE,"E23"),sQuery(id+"F11.wireOp",EDGE,"E24"),sQuery(id+"F11.wireOp",EDGE,"E25"),sQuery(id+"F11.wireOp",EDGE,"E26"),sQuery(id+"F11.wireOp",EDGE,"E27"),sQuery(id+"F11.wireOp",EDGE,"E28"),sQuery(id+"F11.wireOp",EDGE,"E29"),sQuery(id+"F11.wireOp",EDGE,"E30"),sQuery(id+"F11.wireOp",EDGE,"E31")])],"isStart":true}),"instanceName":"1"});
            var sketch = newSketch(context, id + "F133", { "sketchPlane" : qUnion([Q0])});
            skCircle(sketch, "E190.0", {"center": v(-67.53, 25.85) * mm, "radius": 2.35 * mm});
            skCircle(sketch, "E191.0", {"center": v(67.53, -25.85) * mm, "radius": 2.35 * mm});
            skSolve(sketch);
        }
        {
            var Q0;
            Q0 = qSketchRegion(id + "F133", true);
            extrude(context, id + "F134", {"entities" : qUnion([Q0]), "operationType" : NewBodyOperationType.REMOVE, "oppositeDirection" : true, "depth" : (getVariable(context, 'thick')) * mm});
        }
        {
            var Q0;
            Q0=makeQuery(id+"F81.opPattern","COPY",FACE,{"derivedFrom":makeQuery(id+"F8.opExtrude","CAP_FACE",FACE,{"disambiguationData":[OSD([sQuery(id+"F7.wireOp",EDGE,"E12"),sQuery(id+"F7.wireOp",EDGE,"E13"),sQuery(id+"F7.wireOp",EDGE,"E14"),sQuery(id+"F7.wireOp",EDGE,"E15"),sQuery(id+"F7.wireOp",EDGE,"E16"),sQuery(id+"F7.wireOp",EDGE,"E17"),sQuery(id+"F7.wireOp",EDGE,"E18"),sQuery(id+"F7.wireOp",EDGE,"E19"),sQuery(id+"F7.wireOp",EDGE,"E20"),sQuery(id+"F7.wireOp",EDGE,"E21")])],"isStart":true}),"instanceName":"1"});
            var sketch = newSketch(context, id + "F135", { "sketchPlane" : qUnion([Q0])});
            skCircle(sketch, "E192.0", {"center": v(-59.5, 23.5) * mm, "radius": 2.35 * mm});
            skCircle(sketch, "E193.0", {"center": v(59.5, -23.5) * mm, "radius": 2.35 * mm});
            skSolve(sketch);
        }
        {
            var Q0;
            Q0 = qSketchRegion(id + "F135", true);
            extrude(context, id + "F136", {"entities" : qUnion([Q0]), "operationType" : NewBodyOperationType.REMOVE, "oppositeDirection" : true, "depth" : (getVariable(context, 'thick')) * mm});
        }
    });
